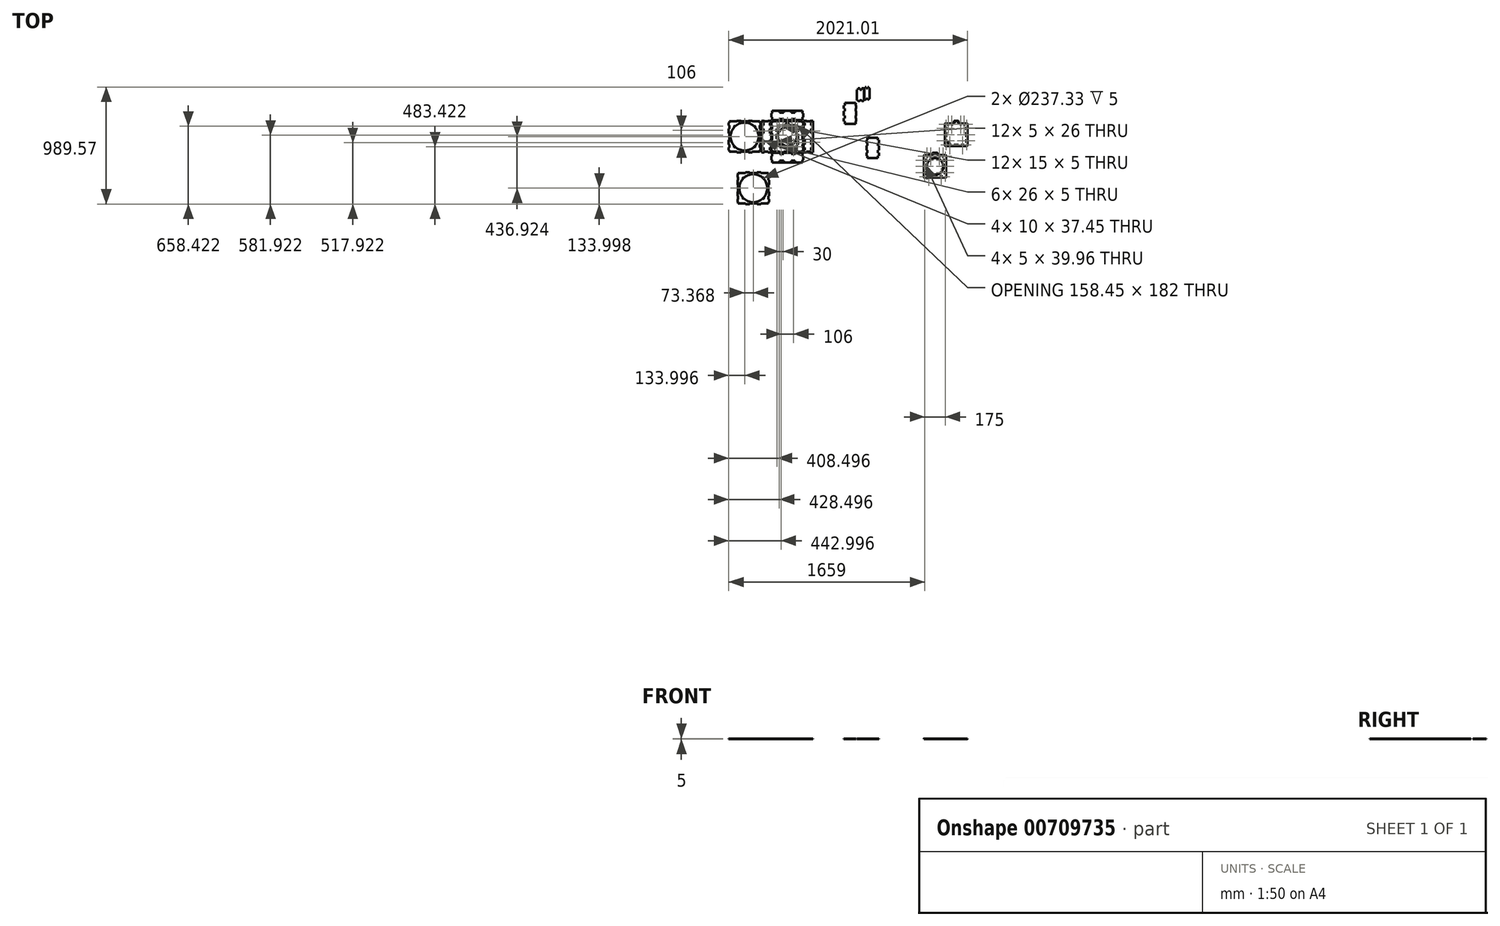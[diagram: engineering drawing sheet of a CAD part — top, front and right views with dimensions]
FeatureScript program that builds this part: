
annotation { "Feature Type Name" : "Feature", "Feature Type Description" : "" }
export const myFeature = defineFeature(function(context is Context, id is Id, definition is map)
    precondition{}
    {
        {
            var Q0;
            Q0=qCreatedBy(makeId("Top.planeOp"),FACE);
            var sketch = newSketch(context, id + "F0", { "sketchPlane" : qUnion([Q0])});
            skPoint(sketch, "E0.endSnap0", {"position": v(-875.61, -634.44) * mm});
            skArc(sketch, "E1", {"start": v(-897.61, -691.52) * mm, "mid": v(-875.61, -848.44) * mm, "end": v(-853.61, -691.52) * mm});
            skPoint(sketch, "E0.start.orphan", {"position": v(-1009.61, -768.44) * mm});
            skLineSegment(sketch, "E2", {"start": v(-875.61, -666.44) * mm, "end": v(-870.73, -666.44) * mm});
            skLineSegment(sketch, "E3", {"start": v(-875.61, -666.44) * mm, "end": v(-853.61, -666.44) * mm});
            skLineSegment(sketch, "E4", {"start": v(-853.61, -666.44) * mm, "end": v(-853.61, -691.52) * mm});
            skLineSegment(sketch, "E5", {"start": v(-897.61, -666.44) * mm, "end": v(-897.61, -691.52) * mm});
            skPoint(sketch, "E6.orphan", {"position": v(-1004.61, -634.44) * mm});
            skLineSegment(sketch, "E7", {"start": v(-1004.61, -625.24) * mm, "end": v(-1004.61, -620.24) * mm});
            skLineSegment(sketch, "E8", {"start": v(-1004.61, -565.24) * mm, "end": v(-1004.61, -555.24) * mm});
            skLineSegment(sketch, "E9", {"start": v(-746.61, -625.24) * mm, "end": v(-746.61, -604) * mm});
            skLineSegment(sketch, "E10", {"start": v(-907.86, -620.24) * mm, "end": v(-940.11, -620.24) * mm});
            skLineSegment(sketch, "E11", {"start": v(-940.11, -620.24) * mm, "end": v(-907.86, -620.24) * mm});
            skPoint(sketch, "E12.end.orphan", {"position": v(-746.61, -634.44) * mm});
            skLineSegment(sketch, "E13", {"start": v(-843.36, -620.24) * mm, "end": v(-811.11, -620.24) * mm});
            skLineSegment(sketch, "E14", {"start": v(-940.11, -620.24) * mm, "end": v(-940.11, -625.24) * mm});
            skLineSegment(sketch, "E15", {"start": v(-811.11, -620.24) * mm, "end": v(-811.11, -625.24) * mm});
            skLineSegment(sketch, "E16", {"start": v(-907.86, -620.24) * mm, "end": v(-907.86, -625.24) * mm});
            skLineSegment(sketch, "E17", {"start": v(-843.36, -620.24) * mm, "end": v(-843.36, -625.24) * mm});
            skLineSegment(sketch, "E18", {"start": v(-940.11, -634.44) * mm, "end": v(-940.11, -639.44) * mm});
            skLineSegment(sketch, "E19", {"start": v(-907.86, -634.44) * mm, "end": v(-907.86, -639.44) * mm});
            skLineSegment(sketch, "E20", {"start": v(-811.11, -634.44) * mm, "end": v(-811.11, -639.44) * mm});
            skLineSegment(sketch, "E21.trimOffspring", {"start": v(-940.11, -634.44) * mm, "end": v(-907.86, -634.44) * mm});
            skLineSegment(sketch, "E22.trimOffspring", {"start": v(-843.36, -634.44) * mm, "end": v(-811.11, -634.44) * mm});
            skPoint(sketch, "E23.orphan", {"position": v(-746.61, -620.24) * mm});
            skPoint(sketch, "E24.orphan", {"position": v(-1004.61, -620.24) * mm});
            skLineSegment(sketch, "E25.MirrorCS", {"start": v(-940.11, -916.63) * mm, "end": v(-940.11, -911.63) * mm});
            skLineSegment(sketch, "E26.MirrorCS", {"start": v(-907.86, -916.63) * mm, "end": v(-907.86, -911.63) * mm});
            skLineSegment(sketch, "E27.MirrorCS", {"start": v(-811.11, -916.63) * mm, "end": v(-811.11, -911.63) * mm});
            skLineSegment(sketch, "E28.MirrorCS", {"start": v(-843.36, -916.63) * mm, "end": v(-843.36, -911.63) * mm});
            skLineSegment(sketch, "E29.MirrorCS", {"start": v(-907.86, -916.63) * mm, "end": v(-940.11, -916.63) * mm});
            skLineSegment(sketch, "E30.MirrorCS", {"start": v(-1004.61, -971.63) * mm, "end": v(-1004.61, -981.63) * mm});
            skPoint(sketch, "E31.MirrorP", {"position": v(-1004.61, -902.44) * mm});
            skPoint(sketch, "E32.MirrorP", {"position": v(-746.61, -902.44) * mm});
            skPoint(sketch, "E33.MirrorP", {"position": v(-875.61, -911.63) * mm});
            skLineSegment(sketch, "E34.MirrorCS", {"start": v(-940.11, -916.63) * mm, "end": v(-907.86, -916.63) * mm});
            skPoint(sketch, "E35.MirrorP", {"position": v(-875.61, -902.44) * mm});
            skPoint(sketch, "E36.MirrorP", {"position": v(-746.61, -916.63) * mm});
            skPoint(sketch, "E37.MirrorP", {"position": v(-875.61, -916.63) * mm});
            skLineSegment(sketch, "E38.MirrorCS", {"start": v(-1004.61, -911.63) * mm, "end": v(-1004.61, -932.88) * mm});
            skPoint(sketch, "E39.MirrorP", {"position": v(-1004.61, -916.63) * mm});
            skLineSegment(sketch, "E40", {"start": v(-940.11, -902.44) * mm, "end": v(-940.11, -897.44) * mm});
            skLineSegment(sketch, "E41", {"start": v(-907.86, -902.44) * mm, "end": v(-907.86, -897.44) * mm});
            skLineSegment(sketch, "E42.trimOffspring", {"start": v(-843.36, -902.44) * mm, "end": v(-811.11, -902.44) * mm});
            skLineSegment(sketch, "E43.trimOffspring", {"start": v(-940.11, -897.44) * mm, "end": v(-1004.61, -897.44) * mm});
            skLineSegment(sketch, "E44", {"start": v(-907.86, -897.44) * mm, "end": v(-843.36, -897.44) * mm});
            skLineSegment(sketch, "E45", {"start": v(-843.36, -897.44) * mm, "end": v(-843.36, -902.44) * mm});
            skLineSegment(sketch, "E46", {"start": v(-811.11, -902.44) * mm, "end": v(-811.11, -897.44) * mm});
            skLineSegment(sketch, "E47", {"start": v(-811.11, -897.44) * mm, "end": v(-746.61, -897.44) * mm});
            skLineSegment(sketch, "E48.trimOffspring", {"start": v(-940.11, -902.44) * mm, "end": v(-907.86, -902.44) * mm});
            skLineSegment(sketch, "E49", {"start": v(-1022.61, -634.44) * mm, "end": v(-1038.86, -634.44) * mm});
            skLineSegment(sketch, "E50", {"start": v(-1022.61, -902.44) * mm, "end": v(-1038.86, -902.44) * mm});
            skPoint(sketch, "E51.start.orphan", {"position": v(-1017.61, -634.44) * mm});
            skPoint(sketch, "E52.end.orphan", {"position": v(-1004.61, -768.49) * mm});
            skLineSegment(sketch, "E53", {"start": v(-1004.61, -788.44) * mm, "end": v(-1004.61, -748.44) * mm});
            skLineSegment(sketch, "E54.trimOffspring", {"start": v(-1009.61, -797.41) * mm, "end": v(-1009.61, -818.44) * mm});
            skPoint(sketch, "E55.start.orphan", {"position": v(-1007.11, -788.44) * mm});
            skLineSegment(sketch, "E56", {"start": v(-1055.11, -639.54) * mm, "end": v(-1071.36, -639.54) * mm});
            skLineSegment(sketch, "E57", {"start": v(-1071.36, -639.54) * mm, "end": v(-1038.86, -639.54) * mm});
            skLineSegment(sketch, "E58", {"start": v(-1038.86, -639.54) * mm, "end": v(-1055.11, -639.54) * mm});
            skLineSegment(sketch, "E59", {"start": v(-1038.86, -639.54) * mm, "end": v(-1038.86, -634.44) * mm});
            skLineSegment(sketch, "E60", {"start": v(-1071.36, -639.54) * mm, "end": v(-1055.11, -639.54) * mm});
            skLineSegment(sketch, "E61", {"start": v(-1071.36, -639.54) * mm, "end": v(-1071.36, -634.44) * mm});
            skLineSegment(sketch, "E62.trimOffspring", {"start": v(-1071.36, -634.44) * mm, "end": v(-1087.61, -634.44) * mm});
            skPoint(sketch, "E63.orphan", {"position": v(-1087.61, -639.54) * mm});
            skPoint(sketch, "E64.orphan", {"position": v(-1022.61, -639.54) * mm});
            skLineSegment(sketch, "E65", {"start": v(-1004.61, -620.24) * mm, "end": v(-1004.61, -604) * mm});
            skLineSegment(sketch, "E66", {"start": v(-1004.61, -604) * mm, "end": v(-1009.61, -604) * mm});
            skLineSegment(sketch, "E67", {"start": v(-1009.61, -604) * mm, "end": v(-1009.61, -571.5) * mm});
            skLineSegment(sketch, "E68", {"start": v(-1009.61, -571.5) * mm, "end": v(-1004.61, -571.5) * mm});
            skLineSegment(sketch, "E69.trimOffspring", {"start": v(-1004.61, -571.5) * mm, "end": v(-1004.61, -565.24) * mm});
            skLineSegment(sketch, "E70.MirrorCS", {"start": v(-1004.61, -932.88) * mm, "end": v(-1009.61, -932.88) * mm});
            skLineSegment(sketch, "E71.MirrorCS", {"start": v(-1009.61, -932.88) * mm, "end": v(-1009.61, -965.38) * mm});
            skLineSegment(sketch, "E72.MirrorCS", {"start": v(-1009.61, -965.38) * mm, "end": v(-1004.61, -965.38) * mm});
            skLineSegment(sketch, "E73.MirrorCS", {"start": v(-1071.36, -897.44) * mm, "end": v(-1038.86, -897.44) * mm});
            skLineSegment(sketch, "E74.MirrorCS", {"start": v(-1071.36, -897.44) * mm, "end": v(-1071.36, -902.44) * mm});
            skLineSegment(sketch, "E75.MirrorCS", {"start": v(-1038.86, -897.44) * mm, "end": v(-1038.86, -902.44) * mm});
            skLineSegment(sketch, "E76.trimOffspring", {"start": v(-1071.36, -902.44) * mm, "end": v(-1087.61, -902.44) * mm});
            skLineSegment(sketch, "E77", {"start": v(-1237.61, -646.69) * mm, "end": v(-1237.61, -644.69) * mm});
            skCircle(sketch, "E78", {"center": v(-1237.61, -644.69) * mm, "radius": 2 * mm});
            skCircle(sketch, "E79", {"center": v(-1237.61, -892.19) * mm, "radius": 2 * mm});
            skCircle(sketch, "E80", {"center": v(-1325.12, -680.93) * mm, "radius": 2 * mm});
            skCircle(sketch, "E81.MirrorC", {"center": v(-1325.12, -855.94) * mm, "radius": 2 * mm});
            skPoint(sketch, "E82.orphan", {"position": v(-1237.61, -768.44) * mm});
            skLineSegment(sketch, "E83.trimOffspring", {"start": v(-1004.61, -965.38) * mm, "end": v(-1004.61, -971.63) * mm});
            skLineSegment(sketch, "E84", {"start": v(-1087.61, -702.02) * mm, "end": v(-1082.61, -702.02) * mm});
            skLineSegment(sketch, "E85", {"start": v(-1087.61, -739.46) * mm, "end": v(-1082.61, -739.46) * mm});
            skLineSegment(sketch, "E86", {"start": v(-1087.61, -884.78) * mm, "end": v(-1082.61, -884.78) * mm});
            skLineSegment(sketch, "E87", {"start": v(-1087.61, -834.86) * mm, "end": v(-1082.61, -834.86) * mm});
            skLineSegment(sketch, "E88", {"start": v(-1087.61, -797.41) * mm, "end": v(-1082.61, -797.41) * mm});
            skLineSegment(sketch, "E89", {"start": v(-1087.61, -862.25) * mm, "end": v(-1082.61, -862.25) * mm});
            skPoint(sketch, "E90.orphan", {"position": v(-1082.61, -902.44) * mm});
            skLineSegment(sketch, "E91.MirrorCS", {"start": v(-741.61, -604) * mm, "end": v(-741.61, -571.5) * mm});
            skLineSegment(sketch, "E92.MirrorCS", {"start": v(-746.61, -604) * mm, "end": v(-741.61, -604) * mm});
            skLineSegment(sketch, "E93.MirrorCS", {"start": v(-741.61, -571.5) * mm, "end": v(-746.61, -571.5) * mm});
            skLineSegment(sketch, "E94.trimOffspring", {"start": v(-746.61, -571.5) * mm, "end": v(-746.61, -555.24) * mm});
            skLineSegment(sketch, "E95.MirrorCS", {"start": v(-1366.61, -897.44) * mm, "end": v(-1302.11, -897.44) * mm});
            skLineSegment(sketch, "E96.MirrorCS", {"start": v(-1302.11, -902.44) * mm, "end": v(-1302.11, -897.44) * mm});
            skLineSegment(sketch, "E97.MirrorCS", {"start": v(-1302.11, -902.44) * mm, "end": v(-1269.86, -902.44) * mm});
            skLineSegment(sketch, "E98.MirrorCS", {"start": v(-1269.86, -902.44) * mm, "end": v(-1269.86, -897.44) * mm});
            skPoint(sketch, "E99.orphan", {"position": v(-1237.61, -736.59) * mm});
            skLineSegment(sketch, "E100", {"start": v(-940.11, -560.24) * mm, "end": v(-940.11, -555.24) * mm});
            skLineSegment(sketch, "E101", {"start": v(-907.86, -560.24) * mm, "end": v(-907.86, -555.24) * mm});
            skLineSegment(sketch, "E102", {"start": v(-811.11, -560.24) * mm, "end": v(-811.11, -555.24) * mm});
            skLineSegment(sketch, "E103", {"start": v(-843.36, -560.24) * mm, "end": v(-843.36, -555.24) * mm});
            skPoint(sketch, "E104.orphan", {"position": v(-747.11, -560.24) * mm});
            skPoint(sketch, "E105.MirrorP", {"position": v(-746.61, -768.44) * mm});
            skLineSegment(sketch, "E106.MirrorCS", {"start": v(-746.61, -911.63) * mm, "end": v(-746.61, -932.88) * mm});
            skLineSegment(sketch, "E107.MirrorCS", {"start": v(-746.61, -965.38) * mm, "end": v(-746.61, -981.63) * mm});
            skLineSegment(sketch, "E108.MirrorCS", {"start": v(-811.11, -976.63) * mm, "end": v(-811.11, -981.63) * mm});
            skLineSegment(sketch, "E109.MirrorCS", {"start": v(-907.86, -976.63) * mm, "end": v(-907.86, -981.63) * mm});
            skLineSegment(sketch, "E110.MirrorCS", {"start": v(-843.36, -976.63) * mm, "end": v(-843.36, -981.63) * mm});
            skLineSegment(sketch, "E111.MirrorCS", {"start": v(-940.11, -976.63) * mm, "end": v(-940.11, -981.63) * mm});
            skPoint(sketch, "E112.MirrorP", {"position": v(-1017.61, -902.44) * mm});
            skPoint(sketch, "E113.MirrorP", {"position": v(-747.11, -916.63) * mm});
            skPoint(sketch, "E114.MirrorP", {"position": v(-1087.61, -897.44) * mm});
            skLineSegment(sketch, "E115.MirrorCS", {"start": v(-741.61, -932.88) * mm, "end": v(-741.61, -965.38) * mm});
            skPoint(sketch, "E116.MirrorP", {"position": v(-1022.61, -897.44) * mm});
            skPoint(sketch, "E117.MirrorP", {"position": v(-1055.11, -902.44) * mm});
            skPoint(sketch, "E118.MirrorP", {"position": v(-746.61, -976.63) * mm});
            skLineSegment(sketch, "E119.MirrorCS", {"start": v(-747.11, -911.63) * mm, "end": v(-746.61, -911.63) * mm});
            skLineSegment(sketch, "E120.trimOffspring", {"start": v(-741.61, -718.44) * mm, "end": v(-741.61, -739.46) * mm});
            skLineSegment(sketch, "E121.trimOffspring", {"start": v(-746.61, -788.34) * mm, "end": v(-746.61, -748.44) * mm});
            skPoint(sketch, "E122.end.orphan", {"position": v(-875.61, -736.59) * mm});
            skPoint(sketch, "E123.end.orphan", {"position": v(-911.85, -768.44) * mm});
            skLineSegment(sketch, "E124.trimOffspring", {"start": v(-1004.61, -571.5) * mm, "end": v(-1004.61, -555.24) * mm});
            skPoint(sketch, "E125.trimOffspring.end.orphan", {"position": v(-1017.61, -678.44) * mm});
            skPoint(sketch, "E126.start.orphan", {"position": v(-1056.61, -736.59) * mm});
            skPoint(sketch, "E127.end.orphan", {"position": v(-1022.61, -818.44) * mm});
            skPoint(sketch, "E128.start.orphan", {"position": v(-1009.61, -718.44) * mm});
            skPoint(sketch, "E129.end.orphan", {"position": v(-1022.61, -718.44) * mm});
            skLineSegment(sketch, "E130", {"start": v(-875.61, -768.44) * mm, "end": v(-875.61, -736.59) * mm});
            skLineSegment(sketch, "E131.MirrorCS", {"start": v(-1009.61, -788.34) * mm, "end": v(-1009.61, -788.44) * mm});
            skLineSegment(sketch, "E132.MirrorCS", {"start": v(-1004.61, -788.34) * mm, "end": v(-1004.61, -748.44) * mm});
            skLineSegment(sketch, "E133.MirrorCS", {"start": v(-1087.61, -652.1) * mm, "end": v(-1082.61, -652.1) * mm});
            skLineSegment(sketch, "E134.MirrorCS", {"start": v(-1087.61, -674.63) * mm, "end": v(-1082.61, -674.63) * mm});
            skLineSegment(sketch, "E135", {"start": v(-1366.61, -674.63) * mm, "end": v(-1366.61, -702.02) * mm});
            skLineSegment(sketch, "E136", {"start": v(-1366.61, -702.02) * mm, "end": v(-1371.61, -702.02) * mm});
            skLineSegment(sketch, "E137", {"start": v(-1371.61, -702.02) * mm, "end": v(-1371.61, -739.46) * mm});
            skLineSegment(sketch, "E138", {"start": v(-1371.61, -739.46) * mm, "end": v(-1366.61, -739.46) * mm});
            skLineSegment(sketch, "E139", {"start": v(-1366.61, -739.46) * mm, "end": v(-1366.61, -797.41) * mm});
            skLineSegment(sketch, "E140", {"start": v(-1366.61, -797.41) * mm, "end": v(-1371.61, -797.41) * mm});
            skLineSegment(sketch, "E141", {"start": v(-1371.61, -797.41) * mm, "end": v(-1371.61, -834.86) * mm});
            skLineSegment(sketch, "E142", {"start": v(-1371.61, -834.86) * mm, "end": v(-1366.61, -834.86) * mm});
            skLineSegment(sketch, "E143", {"start": v(-1366.61, -834.86) * mm, "end": v(-1366.61, -862.25) * mm});
            skLineSegment(sketch, "E144", {"start": v(-1366.61, -862.25) * mm, "end": v(-1371.61, -862.25) * mm});
            skLineSegment(sketch, "E145", {"start": v(-1371.61, -862.25) * mm, "end": v(-1371.61, -884.78) * mm});
            skLineSegment(sketch, "E146", {"start": v(-1371.61, -884.78) * mm, "end": v(-1366.61, -884.78) * mm});
            skLineSegment(sketch, "E147", {"start": v(-1366.61, -884.78) * mm, "end": v(-1366.61, -897.44) * mm});
            skLineSegment(sketch, "E148", {"start": v(-1237.61, -768.44) * mm, "end": v(-1237.61, -748.8) * mm});
            skLineSegment(sketch, "E149.MirrorCS", {"start": v(-1108.61, -674.63) * mm, "end": v(-1108.61, -702.02) * mm});
            skLineSegment(sketch, "E150.MirrorCS", {"start": v(-1108.61, -702.02) * mm, "end": v(-1103.61, -702.02) * mm});
            skLineSegment(sketch, "E151.MirrorCS", {"start": v(-1103.61, -702.02) * mm, "end": v(-1103.61, -739.46) * mm});
            skLineSegment(sketch, "E152.MirrorCS", {"start": v(-1103.61, -739.46) * mm, "end": v(-1108.61, -739.46) * mm});
            skLineSegment(sketch, "E153.MirrorCS", {"start": v(-1108.61, -739.46) * mm, "end": v(-1108.61, -797.41) * mm});
            skLineSegment(sketch, "E154.MirrorCS", {"start": v(-1108.61, -797.41) * mm, "end": v(-1103.61, -797.41) * mm});
            skLineSegment(sketch, "E155.MirrorCS", {"start": v(-1103.61, -797.41) * mm, "end": v(-1103.61, -834.86) * mm});
            skLineSegment(sketch, "E156.MirrorCS", {"start": v(-1103.61, -834.86) * mm, "end": v(-1108.61, -834.86) * mm});
            skLineSegment(sketch, "E157.MirrorCS", {"start": v(-1108.61, -834.86) * mm, "end": v(-1108.61, -862.25) * mm});
            skLineSegment(sketch, "E158.MirrorCS", {"start": v(-1108.61, -862.25) * mm, "end": v(-1103.61, -862.25) * mm});
            skLineSegment(sketch, "E159.MirrorCS", {"start": v(-1103.61, -862.25) * mm, "end": v(-1103.61, -884.78) * mm});
            skLineSegment(sketch, "E160.MirrorCS", {"start": v(-1103.61, -884.78) * mm, "end": v(-1108.61, -884.78) * mm});
            skLineSegment(sketch, "E161.MirrorCS", {"start": v(-1108.61, -897.44) * mm, "end": v(-1173.11, -897.44) * mm});
            skLineSegment(sketch, "E162.MirrorCS", {"start": v(-1173.11, -902.44) * mm, "end": v(-1173.11, -897.44) * mm});
            skLineSegment(sketch, "E163.MirrorCS", {"start": v(-1173.11, -902.44) * mm, "end": v(-1205.36, -902.44) * mm});
            skLineSegment(sketch, "E164.MirrorCS", {"start": v(-1205.36, -902.44) * mm, "end": v(-1205.36, -897.44) * mm});
            skLineSegment(sketch, "E165", {"start": v(-1269.86, -897.44) * mm, "end": v(-1205.36, -897.44) * mm});
            skLineSegment(sketch, "E166", {"start": v(-1108.61, -884.78) * mm, "end": v(-1108.61, -897.44) * mm});
            skCircle(sketch, "E167", {"center": v(-940.63, -837.56) * mm, "radius": 7.1 * mm});
            skLineSegment(sketch, "E168", {"start": v(-1237.61, -768.44) * mm, "end": v(-1301.14, -768.44) * mm});
            skLineSegment(sketch, "E169.MirrorCS", {"start": v(-1371.61, -652.1) * mm, "end": v(-1366.61, -652.1) * mm});
            skLineSegment(sketch, "E170.MirrorCS", {"start": v(-1366.61, -674.63) * mm, "end": v(-1371.61, -674.63) * mm});
            skLineSegment(sketch, "E171.MirrorCS", {"start": v(-1366.61, -702.02) * mm, "end": v(-1366.61, -674.63) * mm});
            skLineSegment(sketch, "E172.MirrorCS", {"start": v(-1366.61, -652.1) * mm, "end": v(-1366.61, -639.44) * mm});
            skLineSegment(sketch, "E173.MirrorCS", {"start": v(-1366.61, -639.44) * mm, "end": v(-1302.11, -639.44) * mm});
            skLineSegment(sketch, "E174.MirrorCS", {"start": v(-1302.11, -634.44) * mm, "end": v(-1302.11, -639.44) * mm});
            skLineSegment(sketch, "E175.MirrorCS", {"start": v(-1302.11, -634.44) * mm, "end": v(-1269.86, -634.44) * mm});
            skLineSegment(sketch, "E176.MirrorCS", {"start": v(-1173.11, -634.44) * mm, "end": v(-1205.36, -634.44) * mm});
            skLineSegment(sketch, "E177.MirrorCS", {"start": v(-1173.11, -634.44) * mm, "end": v(-1173.11, -639.44) * mm});
            skLineSegment(sketch, "E178.MirrorCS", {"start": v(-1108.61, -639.44) * mm, "end": v(-1173.11, -639.44) * mm});
            skLineSegment(sketch, "E179.MirrorCS", {"start": v(-1108.61, -652.1) * mm, "end": v(-1108.61, -639.44) * mm});
            skLineSegment(sketch, "E180.MirrorCS", {"start": v(-1103.61, -652.1) * mm, "end": v(-1108.61, -652.1) * mm});
            skLineSegment(sketch, "E181.MirrorCS", {"start": v(-1103.61, -674.63) * mm, "end": v(-1103.61, -652.1) * mm});
            skLineSegment(sketch, "E182.MirrorCS", {"start": v(-1108.61, -674.63) * mm, "end": v(-1103.61, -674.63) * mm});
            skLineSegment(sketch, "E183.MirrorCS", {"start": v(-1108.61, -702.02) * mm, "end": v(-1108.61, -674.63) * mm});
            skLineSegment(sketch, "E184.MirrorCS", {"start": v(-1103.61, -702.02) * mm, "end": v(-1108.61, -702.02) * mm});
            skLineSegment(sketch, "E185.MirrorCS", {"start": v(-1103.61, -739.46) * mm, "end": v(-1103.61, -702.02) * mm});
            skLineSegment(sketch, "E186.MirrorCS", {"start": v(-1269.86, -639.44) * mm, "end": v(-1205.36, -639.44) * mm});
            skLineSegment(sketch, "E187.MirrorCS", {"start": v(-1269.86, -634.44) * mm, "end": v(-1269.86, -639.44) * mm});
            skLineSegment(sketch, "E188.MirrorCS", {"start": v(-1205.36, -634.44) * mm, "end": v(-1205.36, -639.44) * mm});
            skLineSegment(sketch, "E189.MirrorCS", {"start": v(-1371.61, -674.63) * mm, "end": v(-1371.61, -652.1) * mm});
            skCircle(sketch, "E190.MirrorC", {"center": v(-1150.1, -680.93) * mm, "radius": 2 * mm});
            skCircle(sketch, "E191.MirrorC", {"center": v(-1150.1, -855.94) * mm, "radius": 2 * mm});
            skLineSegment(sketch, "E192", {"start": v(-1237.61, -768.44) * mm, "end": v(-1333.51, -768.44) * mm});
            skCircle(sketch, "E193", {"center": v(-1361.36, -768.44) * mm, "radius": 2 * mm});
            skCircle(sketch, "E194", {"center": v(-1237.61, -768.44) * mm, "radius": 118.66 * mm});
            skPoint(sketch, "E195.trimOffspring.end.orphan", {"position": v(-1366.61, -768.44) * mm});
            skCircle(sketch, "E196.MirrorC", {"center": v(-1113.86, -768.44) * mm, "radius": 2 * mm});
            skLineSegment(sketch, "E197", {"start": v(-843.36, -916.63) * mm, "end": v(-811.11, -916.63) * mm});
            skLineSegment(sketch, "E198", {"start": v(-746.61, -965.38) * mm, "end": v(-741.61, -965.38) * mm});
            skLineSegment(sketch, "E199", {"start": v(-746.61, -932.88) * mm, "end": v(-741.61, -932.88) * mm});
            skLineSegment(sketch, "E200", {"start": v(-875.61, -768.44) * mm, "end": v(-844.99, -768.44) * mm});
            skPoint(sketch, "E201.MirrorCS.end.orphan", {"position": v(-747.11, -565.24) * mm});
            skLineSegment(sketch, "E202", {"start": v(-907.86, -639.44) * mm, "end": v(-843.36, -639.44) * mm});
            skPoint(sketch, "E203.orphan", {"position": v(-746.61, -639.54) * mm});
            skLineSegment(sketch, "E204.trimOffspring", {"start": v(-811.11, -639.44) * mm, "end": v(-746.61, -639.44) * mm});
            skLineSegment(sketch, "E205", {"start": v(-843.36, -639.44) * mm, "end": v(-843.36, -634.44) * mm});
            skLineSegment(sketch, "E206", {"start": v(-940.11, -639.44) * mm, "end": v(-1004.61, -639.44) * mm});
            skPoint(sketch, "E207.orphan", {"position": v(-1004.61, -639.54) * mm});
            skLineSegment(sketch, "E208", {"start": v(-940.11, -630.24) * mm, "end": v(-746.61, -630.24) * mm});
            skLineSegment(sketch, "E209.bottom", {"start": v(-746.61, -630.24) * mm, "end": v(-1004.61, -630.24) * mm});
            skLineSegment(sketch, "E209.top", {"start": v(-811.11, -625.24) * mm, "end": v(-843.36, -625.24) * mm});
            skLineSegment(sketch, "E209.left", {"start": v(-746.61, -630.24) * mm, "end": v(-746.61, -625.24) * mm});
            skLineSegment(sketch, "E209.right", {"start": v(-1004.61, -630.24) * mm, "end": v(-1004.61, -625.24) * mm});
            skLineSegment(sketch, "E210.trimOffspring", {"start": v(-907.86, -625.24) * mm, "end": v(-940.11, -625.24) * mm});
            skPoint(sketch, "E211.orphan", {"position": v(-875.61, -625.24) * mm});
            skLineSegment(sketch, "E212.MirrorCS", {"start": v(-907.86, -555.24) * mm, "end": v(-940.11, -555.24) * mm});
            skLineSegment(sketch, "E213.MirrorCS", {"start": v(-746.61, -550.24) * mm, "end": v(-1004.61, -550.24) * mm});
            skLineSegment(sketch, "E214.MirrorCS", {"start": v(-1004.61, -550.24) * mm, "end": v(-1004.61, -555.24) * mm});
            skLineSegment(sketch, "E215.MirrorCS", {"start": v(-746.61, -550.24) * mm, "end": v(-746.61, -555.24) * mm});
            skLineSegment(sketch, "E216.MirrorCS", {"start": v(-811.11, -555.24) * mm, "end": v(-843.36, -555.24) * mm});
            skPoint(sketch, "E217.start.orphan", {"position": v(-940.11, -590.24) * mm});
            skLineSegment(sketch, "E218.MirrorCS", {"start": v(-746.61, -906.63) * mm, "end": v(-1004.61, -906.63) * mm});
            skLineSegment(sketch, "E219.MirrorCS", {"start": v(-907.86, -911.63) * mm, "end": v(-940.11, -911.63) * mm});
            skLineSegment(sketch, "E220.MirrorCS", {"start": v(-1004.61, -906.63) * mm, "end": v(-1004.61, -911.63) * mm});
            skLineSegment(sketch, "E221.MirrorCS", {"start": v(-811.11, -911.63) * mm, "end": v(-843.36, -911.63) * mm});
            skLineSegment(sketch, "E222.MirrorCS", {"start": v(-746.61, -906.63) * mm, "end": v(-746.61, -911.63) * mm});
            skLineSegment(sketch, "E223.MirrorCS", {"start": v(-746.61, -986.63) * mm, "end": v(-746.61, -981.63) * mm});
            skLineSegment(sketch, "E224.MirrorCS", {"start": v(-746.61, -986.63) * mm, "end": v(-1004.61, -986.63) * mm});
            skLineSegment(sketch, "E225.MirrorCS", {"start": v(-811.11, -981.63) * mm, "end": v(-843.36, -981.63) * mm});
            skLineSegment(sketch, "E226.MirrorCS", {"start": v(-907.86, -981.63) * mm, "end": v(-940.11, -981.63) * mm});
            skLineSegment(sketch, "E227.MirrorCS", {"start": v(-1004.61, -986.63) * mm, "end": v(-1004.61, -981.63) * mm});
            skPoint(sketch, "E228.end.orphan", {"position": v(-738.61, -902.44) * mm});
            skLineSegment(sketch, "E229.MirrorCS", {"start": v(-1092.61, -634.44) * mm, "end": v(-1092.61, -902.44) * mm});
            skLineSegment(sketch, "E230.MirrorCS", {"start": v(-1087.61, -634.44) * mm, "end": v(-1092.61, -634.44) * mm});
            skLineSegment(sketch, "E231.MirrorCS", {"start": v(-1087.61, -674.63) * mm, "end": v(-1087.61, -652.1) * mm});
            skLineSegment(sketch, "E232.MirrorCS", {"start": v(-1087.61, -739.46) * mm, "end": v(-1087.61, -702.02) * mm});
            skLineSegment(sketch, "E233.MirrorCS", {"start": v(-1012.61, -858.44) * mm, "end": v(-1012.61, -678.44) * mm});
            skLineSegment(sketch, "E234.MirrorCS", {"start": v(-1087.61, -834.86) * mm, "end": v(-1087.61, -797.41) * mm});
            skLineSegment(sketch, "E235.MirrorCS", {"start": v(-1087.61, -862.25) * mm, "end": v(-1087.61, -884.78) * mm});
            skLineSegment(sketch, "E236.MirrorCS", {"start": v(-1092.61, -902.44) * mm, "end": v(-1087.61, -902.44) * mm});
            skPoint(sketch, "E237.MirrorCS.start.orphan", {"position": v(-1017.61, -748.44) * mm});
            skPoint(sketch, "E238.MirrorCS.start.orphan", {"position": v(-1017.61, -718.44) * mm});
            skLineSegment(sketch, "E239.MirrorCS", {"start": v(-1017.61, -902.44) * mm, "end": v(-1022.61, -902.44) * mm});
            skPoint(sketch, "E240.MirrorCS.end.orphan", {"position": v(-1022.61, -748.44) * mm});
            skLineSegment(sketch, "E241", {"start": v(-1022.61, -652.1) * mm, "end": v(-1017.61, -652.1) * mm});
            skLineSegment(sketch, "E242", {"start": v(-1022.61, -634.44) * mm, "end": v(-1017.61, -634.44) * mm});
            skLineSegment(sketch, "E243", {"start": v(-1012.61, -858.44) * mm, "end": v(-1012.61, -902.44) * mm});
            skPoint(sketch, "E243.endSnap0", {"position": v(-1020.11, -902.44) * mm});
            skLineSegment(sketch, "E244", {"start": v(-1012.61, -902.44) * mm, "end": v(-1022.61, -902.44) * mm});
            skLineSegment(sketch, "E245", {"start": v(-1012.61, -678.44) * mm, "end": v(-1012.61, -634.44) * mm});
            skLineSegment(sketch, "E246", {"start": v(-1012.61, -634.44) * mm, "end": v(-1017.61, -634.44) * mm});
            skLineSegment(sketch, "E247", {"start": v(-1017.61, -652.1) * mm, "end": v(-1017.61, -674.63) * mm});
            skPoint(sketch, "E248.MirrorCS.start.orphan", {"position": v(-1012.61, -858.44) * mm});
            skLineSegment(sketch, "E249", {"start": v(-1022.61, -884.78) * mm, "end": v(-1017.61, -884.78) * mm});
            skLineSegment(sketch, "E250", {"start": v(-1022.61, -862.25) * mm, "end": v(-1017.61, -862.25) * mm});
            skLineSegment(sketch, "E251", {"start": v(-1022.61, -834.86) * mm, "end": v(-1017.61, -834.86) * mm});
            skLineSegment(sketch, "E252", {"start": v(-1022.61, -797.41) * mm, "end": v(-1017.61, -797.41) * mm});
            skLineSegment(sketch, "E253", {"start": v(-1022.61, -739.46) * mm, "end": v(-1017.61, -739.46) * mm});
            skLineSegment(sketch, "E254", {"start": v(-1022.61, -702.02) * mm, "end": v(-1017.61, -702.02) * mm});
            skLineSegment(sketch, "E255", {"start": v(-1022.61, -674.63) * mm, "end": v(-1017.61, -674.63) * mm});
            skPoint(sketch, "E256.orphan", {"position": v(-1022.61, -678.44) * mm});
            skPoint(sketch, "E257.MirrorCS.end.orphan", {"position": v(-1012.61, -678.44) * mm});
            skPoint(sketch, "E258.MirrorCS.start.orphan", {"position": v(-1022.61, -634.44) * mm});
            skPoint(sketch, "E259.MirrorCS.end.orphan", {"position": v(-1022.61, -652.1) * mm});
            skPoint(sketch, "E260.MirrorCS.start.orphan", {"position": v(-1022.61, -674.63) * mm});
            skPoint(sketch, "E261.orphan", {"position": v(-1022.61, -739.46) * mm});
            skPoint(sketch, "E262.MirrorCS.end.orphan", {"position": v(-1022.61, -702.02) * mm});
            skPoint(sketch, "E263.MirrorCS.end.orphan", {"position": v(-1022.61, -797.41) * mm});
            skPoint(sketch, "E264.MirrorCS.end.orphan", {"position": v(-1022.61, -902.44) * mm});
            skLineSegment(sketch, "E265", {"start": v(-1017.61, -862.25) * mm, "end": v(-1017.61, -884.78) * mm});
            skLineSegment(sketch, "E266", {"start": v(-1017.61, -702.02) * mm, "end": v(-1017.61, -718.44) * mm});
            skLineSegment(sketch, "E267", {"start": v(-1082.61, -652.1) * mm, "end": v(-1077.61, -652.1) * mm});
            skLineSegment(sketch, "E268", {"start": v(-1077.61, -652.1) * mm, "end": v(-1077.61, -674.63) * mm});
            skLineSegment(sketch, "E269", {"start": v(-1077.61, -674.63) * mm, "end": v(-1082.61, -674.63) * mm});
            skLineSegment(sketch, "E270", {"start": v(-1082.61, -702.02) * mm, "end": v(-1077.61, -702.02) * mm});
            skLineSegment(sketch, "E271", {"start": v(-1077.61, -702.02) * mm, "end": v(-1077.61, -739.46) * mm});
            skLineSegment(sketch, "E272", {"start": v(-1077.61, -739.46) * mm, "end": v(-1082.61, -739.46) * mm});
            skLineSegment(sketch, "E273", {"start": v(-1082.61, -797.41) * mm, "end": v(-1077.61, -797.41) * mm});
            skLineSegment(sketch, "E274", {"start": v(-1077.61, -797.41) * mm, "end": v(-1077.61, -834.86) * mm});
            skLineSegment(sketch, "E275", {"start": v(-1077.61, -834.86) * mm, "end": v(-1082.61, -834.86) * mm});
            skLineSegment(sketch, "E276", {"start": v(-1082.61, -862.25) * mm, "end": v(-1077.61, -862.25) * mm});
            skLineSegment(sketch, "E277", {"start": v(-1077.61, -862.25) * mm, "end": v(-1077.61, -884.78) * mm});
            skLineSegment(sketch, "E278", {"start": v(-1077.61, -884.78) * mm, "end": v(-1082.61, -884.78) * mm});
            skPoint(sketch, "E279.MirrorCS.end.orphan", {"position": v(-1082.61, -674.63) * mm});
            skLineSegment(sketch, "E280", {"start": v(-1022.61, -674.63) * mm, "end": v(-1022.61, -652.1) * mm});
            skLineSegment(sketch, "E281", {"start": v(-1022.61, -702.02) * mm, "end": v(-1022.61, -739.46) * mm});
            skLineSegment(sketch, "E282", {"start": v(-1022.61, -797.41) * mm, "end": v(-1022.61, -834.86) * mm});
            skLineSegment(sketch, "E283", {"start": v(-1022.61, -862.25) * mm, "end": v(-1022.61, -884.78) * mm});
            skPoint(sketch, "E284.MirrorCS.end.orphan", {"position": v(-1027.61, -884.78) * mm});
            skPoint(sketch, "E285.MirrorCS.start.orphan", {"position": v(-1027.61, -862.25) * mm});
            skPoint(sketch, "E286.MirrorCS.end.orphan", {"position": v(-1027.61, -834.86) * mm});
            skPoint(sketch, "E287.MirrorCS.start.orphan", {"position": v(-1027.61, -797.41) * mm});
            skPoint(sketch, "E288.MirrorCS.end.orphan", {"position": v(-1027.61, -652.1) * mm});
            skPoint(sketch, "E289.MirrorCS.end.orphan", {"position": v(-1027.61, -674.63) * mm});
            skPoint(sketch, "E290.MirrorCS.end.orphan", {"position": v(-1027.61, -702.02) * mm});
            skPoint(sketch, "E291.MirrorCS.end.orphan", {"position": v(-1027.61, -739.46) * mm});
            skLineSegment(sketch, "E292", {"start": v(-1009.61, -674.63) * mm, "end": v(-1004.61, -674.63) * mm});
            skLineSegment(sketch, "E293", {"start": v(-1004.61, -674.63) * mm, "end": v(-1004.61, -678.44) * mm});
            skLineSegment(sketch, "E294", {"start": v(-1009.61, -652.1) * mm, "end": v(-1004.61, -652.1) * mm});
            skLineSegment(sketch, "E295", {"start": v(-1004.61, -652.1) * mm, "end": v(-1004.61, -639.44) * mm});
            skPoint(sketch, "E296.orphan", {"position": v(-1009.61, -634.44) * mm});
            skLineSegment(sketch, "E297", {"start": v(-1009.61, -652.1) * mm, "end": v(-1009.61, -674.63) * mm});
            skPoint(sketch, "E298.start.orphan", {"position": v(-1009.61, -678.44) * mm});
            skLineSegment(sketch, "E299", {"start": v(-1009.61, -718.44) * mm, "end": v(-1009.61, -702.02) * mm});
            skLineSegment(sketch, "E300", {"start": v(-1009.61, -702.02) * mm, "end": v(-1004.61, -702.02) * mm});
            skLineSegment(sketch, "E301", {"start": v(-1009.61, -718.44) * mm, "end": v(-1009.61, -739.46) * mm});
            skLineSegment(sketch, "E302", {"start": v(-1009.61, -739.46) * mm, "end": v(-1004.61, -739.46) * mm});
            skLineSegment(sketch, "E303", {"start": v(-1004.61, -739.46) * mm, "end": v(-1004.61, -748.44) * mm});
            skPoint(sketch, "E304.MirrorCS.end.orphan", {"position": v(-1009.61, -748.44) * mm});
            skPoint(sketch, "E304.MirrorCS.start.orphan", {"position": v(-1004.61, -748.44) * mm});
            skPoint(sketch, "E305.orphan", {"position": v(-1004.61, -718.44) * mm});
            skLineSegment(sketch, "E306", {"start": v(-1004.61, -678.44) * mm, "end": v(-1004.61, -702.02) * mm});
            skLineSegment(sketch, "E307", {"start": v(-1009.61, -818.44) * mm, "end": v(-1009.61, -797.41) * mm});
            skLineSegment(sketch, "E308", {"start": v(-1009.61, -797.41) * mm, "end": v(-1004.61, -797.41) * mm});
            skLineSegment(sketch, "E309", {"start": v(-1004.61, -797.41) * mm, "end": v(-1004.61, -788.34) * mm});
            skPoint(sketch, "E310.orphan", {"position": v(-1009.61, -788.44) * mm});
            skPoint(sketch, "E311.MirrorCS.start.orphan", {"position": v(-1009.61, -788.34) * mm});
            skPoint(sketch, "E312.start.orphan", {"position": v(-1009.61, -834.86) * mm});
            skLineSegment(sketch, "E313", {"start": v(-1009.61, -818.44) * mm, "end": v(-1009.61, -834.86) * mm});
            skLineSegment(sketch, "E314", {"start": v(-1009.61, -834.86) * mm, "end": v(-1004.61, -834.86) * mm});
            skPoint(sketch, "E315.MirrorCS.end.orphan", {"position": v(-1004.61, -818.44) * mm});
            skPoint(sketch, "E315.MirrorCS.start.orphan", {"position": v(-1009.61, -818.44) * mm});
            skLineSegment(sketch, "E316", {"start": v(-1017.61, -797.41) * mm, "end": v(-1017.61, -834.86) * mm});
            skLineSegment(sketch, "E317", {"start": v(-1004.61, -834.86) * mm, "end": v(-1004.61, -858.44) * mm});
            skLineSegment(sketch, "E318", {"start": v(-1009.61, -862.25) * mm, "end": v(-1004.61, -862.25) * mm});
            skLineSegment(sketch, "E319", {"start": v(-1004.61, -862.25) * mm, "end": v(-1004.61, -858.44) * mm});
            skLineSegment(sketch, "E320", {"start": v(-1009.61, -862.25) * mm, "end": v(-1009.61, -884.78) * mm});
            skLineSegment(sketch, "E321", {"start": v(-1009.61, -884.78) * mm, "end": v(-1004.61, -884.78) * mm});
            skLineSegment(sketch, "E322", {"start": v(-1004.61, -884.78) * mm, "end": v(-1004.61, -897.44) * mm});
            skPoint(sketch, "E323.orphan", {"position": v(-1009.61, -902.44) * mm});
            skLineSegment(sketch, "E324", {"start": v(-1017.61, -702.02) * mm, "end": v(-1017.61, -739.46) * mm});
            skPoint(sketch, "E325.end.orphan", {"position": v(-738.61, -678.44) * mm});
            skPoint(sketch, "E325.start.orphan", {"position": v(-733.61, -678.44) * mm});
            skPoint(sketch, "E326.end.orphan", {"position": v(-733.61, -718.44) * mm});
            skPoint(sketch, "E326.start.orphan", {"position": v(-733.61, -748.44) * mm});
            skPoint(sketch, "E327.start.orphan", {"position": v(-738.61, -858.44) * mm});
            skLineSegment(sketch, "E328.MirrorCS", {"start": v(-679.86, -639.54) * mm, "end": v(-679.86, -634.44) * mm});
            skLineSegment(sketch, "E329.MirrorCS", {"start": v(-679.86, -897.44) * mm, "end": v(-679.86, -902.44) * mm});
            skLineSegment(sketch, "E330.MirrorCS", {"start": v(-712.36, -639.54) * mm, "end": v(-712.36, -634.44) * mm});
            skLineSegment(sketch, "E331.MirrorCS", {"start": v(-712.36, -897.44) * mm, "end": v(-712.36, -902.44) * mm});
            skPoint(sketch, "E332.MirrorP", {"position": v(-723.61, -884.78) * mm});
            skLineSegment(sketch, "E333.MirrorCS", {"start": v(-668.61, -652.1) * mm, "end": v(-673.61, -652.1) * mm});
            skLineSegment(sketch, "E334.MirrorCS", {"start": v(-673.61, -739.46) * mm, "end": v(-668.61, -739.46) * mm});
            skPoint(sketch, "E335.MirrorP", {"position": v(-723.61, -674.63) * mm});
            skLineSegment(sketch, "E336.MirrorCS", {"start": v(-668.61, -702.02) * mm, "end": v(-673.61, -702.02) * mm});
            skPoint(sketch, "E337.MirrorP", {"position": v(-723.61, -862.25) * mm});
            skLineSegment(sketch, "E338.MirrorCS", {"start": v(-668.61, -797.41) * mm, "end": v(-673.61, -797.41) * mm});
            skLineSegment(sketch, "E339.MirrorCS", {"start": v(-673.61, -674.63) * mm, "end": v(-668.61, -674.63) * mm});
            skLineSegment(sketch, "E340.MirrorCS", {"start": v(-696.11, -639.54) * mm, "end": v(-679.86, -639.54) * mm});
            skLineSegment(sketch, "E341.MirrorCS", {"start": v(-728.61, -902.44) * mm, "end": v(-712.36, -902.44) * mm});
            skLineSegment(sketch, "E342.MirrorCS", {"start": v(-668.61, -862.25) * mm, "end": v(-673.61, -862.25) * mm});
            skLineSegment(sketch, "E343.MirrorCS", {"start": v(-673.61, -834.86) * mm, "end": v(-668.61, -834.86) * mm});
            skLineSegment(sketch, "E344.MirrorCS", {"start": v(-673.61, -884.78) * mm, "end": v(-668.61, -884.78) * mm});
            skPoint(sketch, "E345.MirrorP", {"position": v(-733.61, -902.44) * mm});
            skPoint(sketch, "E346.MirrorP", {"position": v(-723.61, -739.46) * mm});
            skLineSegment(sketch, "E347.MirrorCS", {"start": v(-679.86, -897.44) * mm, "end": v(-712.36, -897.44) * mm});
            skPoint(sketch, "E348.MirrorP", {"position": v(-723.61, -797.41) * mm});
            skLineSegment(sketch, "E349.MirrorCS", {"start": v(-679.86, -639.54) * mm, "end": v(-712.36, -639.54) * mm});
            skPoint(sketch, "E350.MirrorP", {"position": v(-733.61, -634.44) * mm});
            skPoint(sketch, "E351.MirrorP", {"position": v(-723.61, -834.86) * mm});
            skPoint(sketch, "E352.MirrorP", {"position": v(-723.61, -702.02) * mm});
            skPoint(sketch, "E353.MirrorP", {"position": v(-723.61, -652.1) * mm});
            skPoint(sketch, "E354.MirrorP", {"position": v(-694.61, -736.59) * mm});
            skLineSegment(sketch, "E355.MirrorCS", {"start": v(-673.61, -652.1) * mm, "end": v(-673.61, -674.63) * mm});
            skLineSegment(sketch, "E356.MirrorCS", {"start": v(-728.61, -674.63) * mm, "end": v(-728.61, -652.1) * mm});
            skPoint(sketch, "E357.MirrorP", {"position": v(-668.61, -902.44) * mm});
            skLineSegment(sketch, "E358.MirrorCS", {"start": v(-728.61, -702.02) * mm, "end": v(-728.61, -739.46) * mm});
            skLineSegment(sketch, "E359.MirrorCS", {"start": v(-673.61, -862.25) * mm, "end": v(-673.61, -884.78) * mm});
            skLineSegment(sketch, "E360.MirrorCS", {"start": v(-728.61, -797.41) * mm, "end": v(-728.61, -834.86) * mm});
            skLineSegment(sketch, "E361.MirrorCS", {"start": v(-728.61, -862.25) * mm, "end": v(-728.61, -884.78) * mm});
            skLineSegment(sketch, "E362.MirrorCS", {"start": v(-679.86, -639.54) * mm, "end": v(-696.11, -639.54) * mm});
            skLineSegment(sketch, "E363.MirrorCS", {"start": v(-673.61, -702.02) * mm, "end": v(-673.61, -739.46) * mm});
            skLineSegment(sketch, "E364.MirrorCS", {"start": v(-712.36, -639.54) * mm, "end": v(-696.11, -639.54) * mm});
            skLineSegment(sketch, "E365.MirrorCS", {"start": v(-728.61, -634.44) * mm, "end": v(-712.36, -634.44) * mm});
            skPoint(sketch, "E366.MirrorP", {"position": v(-696.11, -902.44) * mm});
            skPoint(sketch, "E367.MirrorP", {"position": v(-668.61, -674.63) * mm});
            skLineSegment(sketch, "E368.MirrorCS", {"start": v(-673.61, -797.41) * mm, "end": v(-673.61, -834.86) * mm});
            skLineSegment(sketch, "E369.MirrorCS", {"start": v(-663.61, -862.25) * mm, "end": v(-668.61, -862.25) * mm});
            skLineSegment(sketch, "E370.MirrorCS", {"start": v(-663.61, -797.41) * mm, "end": v(-668.61, -797.41) * mm});
            skLineSegment(sketch, "E371.MirrorCS", {"start": v(-663.61, -634.44) * mm, "end": v(-658.61, -634.44) * mm});
            skLineSegment(sketch, "E372.MirrorCS", {"start": v(-663.61, -739.46) * mm, "end": v(-668.61, -739.46) * mm});
            skLineSegment(sketch, "E373.MirrorCS", {"start": v(-658.61, -902.44) * mm, "end": v(-663.61, -902.44) * mm});
            skLineSegment(sketch, "E374.MirrorCS", {"start": v(-663.61, -674.63) * mm, "end": v(-668.61, -674.63) * mm});
            skLineSegment(sketch, "E375.MirrorCS", {"start": v(-663.61, -884.78) * mm, "end": v(-668.61, -884.78) * mm});
            skLineSegment(sketch, "E376.MirrorCS", {"start": v(-663.61, -834.86) * mm, "end": v(-668.61, -834.86) * mm});
            skLineSegment(sketch, "E377.MirrorCS", {"start": v(-663.61, -652.1) * mm, "end": v(-668.61, -652.1) * mm});
            skLineSegment(sketch, "E378.MirrorCS", {"start": v(-663.61, -702.02) * mm, "end": v(-668.61, -702.02) * mm});
            skLineSegment(sketch, "E379.MirrorCS", {"start": v(-663.61, -862.25) * mm, "end": v(-663.61, -884.78) * mm});
            skPoint(sketch, "E380.MirrorP", {"position": v(-663.61, -639.54) * mm});
            skLineSegment(sketch, "E381.MirrorCS", {"start": v(-663.61, -739.46) * mm, "end": v(-663.61, -702.02) * mm});
            skPoint(sketch, "E382.MirrorP", {"position": v(-663.61, -897.44) * mm});
            skLineSegment(sketch, "E383.MirrorCS", {"start": v(-658.61, -634.44) * mm, "end": v(-658.61, -902.44) * mm});
            skLineSegment(sketch, "E384.MirrorCS", {"start": v(-663.61, -674.63) * mm, "end": v(-663.61, -674.63) * mm});
            skLineSegment(sketch, "E385.MirrorCS", {"start": v(-663.61, -674.63) * mm, "end": v(-663.61, -652.1) * mm});
            skLineSegment(sketch, "E386.MirrorCS", {"start": v(-663.61, -834.86) * mm, "end": v(-663.61, -797.41) * mm});
            skLineSegment(sketch, "E387.MirrorCS", {"start": v(-733.61, -902.44) * mm, "end": v(-728.61, -902.44) * mm});
            skPoint(sketch, "E388.MirrorP", {"position": v(-741.61, -718.44) * mm});
            skLineSegment(sketch, "E389.MirrorCS", {"start": v(-728.61, -674.63) * mm, "end": v(-733.61, -674.63) * mm});
            skLineSegment(sketch, "E390.MirrorCS", {"start": v(-728.61, -834.86) * mm, "end": v(-733.61, -834.86) * mm});
            skLineSegment(sketch, "E391.MirrorCS", {"start": v(-733.61, -702.02) * mm, "end": v(-733.61, -718.44) * mm});
            skLineSegment(sketch, "E392.MirrorCS", {"start": v(-728.61, -862.25) * mm, "end": v(-733.61, -862.25) * mm});
            skLineSegment(sketch, "E393.MirrorCS", {"start": v(-728.61, -652.1) * mm, "end": v(-733.61, -652.1) * mm});
            skLineSegment(sketch, "E394.MirrorCS", {"start": v(-728.61, -739.46) * mm, "end": v(-733.61, -739.46) * mm});
            skLineSegment(sketch, "E395.MirrorCS", {"start": v(-728.61, -702.02) * mm, "end": v(-733.61, -702.02) * mm});
            skLineSegment(sketch, "E396.MirrorCS", {"start": v(-728.61, -797.41) * mm, "end": v(-733.61, -797.41) * mm});
            skPoint(sketch, "E397.MirrorP", {"position": v(-728.61, -718.44) * mm});
            skLineSegment(sketch, "E398.MirrorCS", {"start": v(-728.61, -634.44) * mm, "end": v(-733.61, -634.44) * mm});
            skLineSegment(sketch, "E399.MirrorCS", {"start": v(-728.61, -884.78) * mm, "end": v(-733.61, -884.78) * mm});
            skPoint(sketch, "E400.MirrorP", {"position": v(-741.61, -634.44) * mm});
            skPoint(sketch, "E401.MirrorP", {"position": v(-728.61, -897.44) * mm});
            skPoint(sketch, "E402.MirrorP", {"position": v(-728.61, -674.63) * mm});
            skPoint(sketch, "E403.MirrorP", {"position": v(-728.61, -678.44) * mm});
            skPoint(sketch, "E404.MirrorP", {"position": v(-728.61, -702.02) * mm});
            skPoint(sketch, "E405.MirrorP", {"position": v(-728.61, -652.1) * mm});
            skPoint(sketch, "E406.MirrorP", {"position": v(-728.61, -902.44) * mm});
            skPoint(sketch, "E407.MirrorP", {"position": v(-741.61, -678.44) * mm});
            skPoint(sketch, "E408.MirrorP", {"position": v(-741.61, -748.44) * mm});
            skPoint(sketch, "E409.MirrorP", {"position": v(-728.61, -639.54) * mm});
            skPoint(sketch, "E410.MirrorP", {"position": v(-741.61, -902.44) * mm});
            skPoint(sketch, "E411.MirrorP", {"position": v(-728.61, -818.44) * mm});
            skPoint(sketch, "E412.MirrorP", {"position": v(-741.61, -834.86) * mm});
            skLineSegment(sketch, "E413.MirrorCS", {"start": v(-733.61, -797.41) * mm, "end": v(-733.61, -834.86) * mm});
            skPoint(sketch, "E414.MirrorP", {"position": v(-741.61, -818.44) * mm});
            skPoint(sketch, "E415.MirrorP", {"position": v(-731.11, -902.44) * mm});
            skPoint(sketch, "E416.MirrorP", {"position": v(-728.61, -739.46) * mm});
            skPoint(sketch, "E417.MirrorP", {"position": v(-741.61, -768.44) * mm});
            skLineSegment(sketch, "E418.MirrorCS", {"start": v(-733.61, -702.02) * mm, "end": v(-733.61, -739.46) * mm});
            skLineSegment(sketch, "E419.MirrorCS", {"start": v(-733.61, -652.1) * mm, "end": v(-733.61, -674.63) * mm});
            skPoint(sketch, "E420.MirrorP", {"position": v(-728.61, -797.41) * mm});
            skPoint(sketch, "E421.MirrorP", {"position": v(-728.61, -748.44) * mm});
            skPoint(sketch, "E422.MirrorP", {"position": v(-728.61, -634.44) * mm});
            skLineSegment(sketch, "E423.MirrorCS", {"start": v(-733.61, -862.25) * mm, "end": v(-733.61, -884.78) * mm});
            skLineSegment(sketch, "E424.MirrorCS", {"start": v(-738.61, -678.44) * mm, "end": v(-738.61, -634.44) * mm});
            skLineSegment(sketch, "E425.MirrorCS", {"start": v(-738.61, -858.44) * mm, "end": v(-738.61, -678.44) * mm});
            skLineSegment(sketch, "E426", {"start": v(-679.86, -634.44) * mm, "end": v(-663.61, -634.44) * mm});
            skLineSegment(sketch, "E427", {"start": v(-738.61, -634.44) * mm, "end": v(-733.61, -634.44) * mm});
            skLineSegment(sketch, "E428", {"start": v(-679.86, -902.44) * mm, "end": v(-663.61, -902.44) * mm});
            skLineSegment(sketch, "E429", {"start": v(-738.61, -858.44) * mm, "end": v(-738.61, -902.44) * mm});
            skLineSegment(sketch, "E430", {"start": v(-733.61, -902.44) * mm, "end": v(-738.61, -902.44) * mm});
            skPoint(sketch, "E431.MirrorCS.start.orphan", {"position": v(-696.11, -897.44) * mm});
            skPoint(sketch, "E432.start.orphan", {"position": v(-1055.11, -897.44) * mm});
            skLineSegment(sketch, "E433.MirrorCS", {"start": v(-746.61, -652.1) * mm, "end": v(-746.61, -639.44) * mm});
            skLineSegment(sketch, "E434.MirrorCS", {"start": v(-741.61, -652.1) * mm, "end": v(-746.61, -652.1) * mm});
            skLineSegment(sketch, "E435.MirrorCS", {"start": v(-741.61, -652.1) * mm, "end": v(-741.61, -674.63) * mm});
            skLineSegment(sketch, "E436.MirrorCS", {"start": v(-741.61, -674.63) * mm, "end": v(-746.61, -674.63) * mm});
            skLineSegment(sketch, "E437.MirrorCS", {"start": v(-746.61, -678.44) * mm, "end": v(-746.61, -702.02) * mm});
            skLineSegment(sketch, "E438.MirrorCS", {"start": v(-746.61, -674.63) * mm, "end": v(-746.61, -678.44) * mm});
            skLineSegment(sketch, "E439.MirrorCS", {"start": v(-741.61, -702.02) * mm, "end": v(-746.61, -702.02) * mm});
            skLineSegment(sketch, "E440.MirrorCS", {"start": v(-741.61, -718.44) * mm, "end": v(-741.61, -702.02) * mm});
            skLineSegment(sketch, "E441.MirrorCS", {"start": v(-741.61, -739.46) * mm, "end": v(-746.61, -739.46) * mm});
            skLineSegment(sketch, "E442.MirrorCS", {"start": v(-746.61, -739.46) * mm, "end": v(-746.61, -748.44) * mm});
            skLineSegment(sketch, "E443.MirrorCS", {"start": v(-746.61, -797.41) * mm, "end": v(-746.61, -788.34) * mm});
            skLineSegment(sketch, "E444.MirrorCS", {"start": v(-741.61, -797.41) * mm, "end": v(-746.61, -797.41) * mm});
            skLineSegment(sketch, "E445.MirrorCS", {"start": v(-741.61, -797.41) * mm, "end": v(-741.61, -818.44) * mm});
            skLineSegment(sketch, "E446.MirrorCS", {"start": v(-741.61, -834.86) * mm, "end": v(-746.61, -834.86) * mm});
            skLineSegment(sketch, "E447.MirrorCS", {"start": v(-746.61, -834.86) * mm, "end": v(-746.61, -858.44) * mm});
            skLineSegment(sketch, "E448.MirrorCS", {"start": v(-741.61, -862.25) * mm, "end": v(-746.61, -862.25) * mm});
            skLineSegment(sketch, "E449.MirrorCS", {"start": v(-746.61, -862.25) * mm, "end": v(-746.61, -858.44) * mm});
            skLineSegment(sketch, "E450.MirrorCS", {"start": v(-741.61, -862.25) * mm, "end": v(-741.61, -884.78) * mm});
            skLineSegment(sketch, "E451.MirrorCS", {"start": v(-741.61, -884.78) * mm, "end": v(-746.61, -884.78) * mm});
            skLineSegment(sketch, "E452.MirrorCS", {"start": v(-746.61, -884.78) * mm, "end": v(-746.61, -897.44) * mm});
            skLineSegment(sketch, "E453", {"start": v(-741.61, -818.44) * mm, "end": v(-741.61, -834.86) * mm});
            skPoint(sketch, "E454.MirrorCS.end.orphan", {"position": v(-746.61, -818.44) * mm});
            skLineSegment(sketch, "E455", {"start": v(-1164.25, -1083.61) * mm, "end": v(-1164.25, -1081.61) * mm});
            skCircle(sketch, "E456", {"center": v(-1164.25, -1081.61) * mm, "radius": 2 * mm});
            skCircle(sketch, "E457", {"center": v(-1164.25, -1329.11) * mm, "radius": 2 * mm});
            skCircle(sketch, "E458", {"center": v(-1251.75, -1117.86) * mm, "radius": 2 * mm});
            skCircle(sketch, "E459.MirrorC", {"center": v(-1251.75, -1292.87) * mm, "radius": 2 * mm});
            skPoint(sketch, "E460.orphan", {"position": v(-1164.25, -1205.36) * mm});
            skLineSegment(sketch, "E461.MirrorCS", {"start": v(-1293.25, -1334.36) * mm, "end": v(-1228.75, -1334.36) * mm});
            skLineSegment(sketch, "E462.MirrorCS", {"start": v(-1228.75, -1339.36) * mm, "end": v(-1228.75, -1334.36) * mm});
            skLineSegment(sketch, "E463.MirrorCS", {"start": v(-1228.75, -1339.36) * mm, "end": v(-1196.5, -1339.36) * mm});
            skLineSegment(sketch, "E464.MirrorCS", {"start": v(-1196.5, -1339.36) * mm, "end": v(-1196.5, -1334.36) * mm});
            skPoint(sketch, "E465.orphan", {"position": v(-1164.25, -1173.51) * mm});
            skLineSegment(sketch, "E466", {"start": v(-1293.25, -1111.55) * mm, "end": v(-1293.25, -1138.94) * mm});
            skLineSegment(sketch, "E467", {"start": v(-1293.25, -1138.94) * mm, "end": v(-1298.25, -1138.94) * mm});
            skLineSegment(sketch, "E468", {"start": v(-1298.25, -1138.94) * mm, "end": v(-1298.25, -1176.39) * mm});
            skLineSegment(sketch, "E469", {"start": v(-1298.25, -1176.39) * mm, "end": v(-1293.25, -1176.39) * mm});
            skLineSegment(sketch, "E470", {"start": v(-1293.25, -1176.39) * mm, "end": v(-1293.25, -1234.34) * mm});
            skLineSegment(sketch, "E471", {"start": v(-1293.25, -1234.34) * mm, "end": v(-1298.25, -1234.34) * mm});
            skLineSegment(sketch, "E472", {"start": v(-1298.25, -1234.34) * mm, "end": v(-1298.25, -1271.78) * mm});
            skLineSegment(sketch, "E473", {"start": v(-1298.25, -1271.78) * mm, "end": v(-1293.25, -1271.78) * mm});
            skLineSegment(sketch, "E474", {"start": v(-1293.25, -1271.78) * mm, "end": v(-1293.25, -1299.17) * mm});
            skLineSegment(sketch, "E475", {"start": v(-1293.25, -1299.17) * mm, "end": v(-1298.25, -1299.17) * mm});
            skLineSegment(sketch, "E476", {"start": v(-1298.25, -1299.17) * mm, "end": v(-1298.25, -1321.7) * mm});
            skLineSegment(sketch, "E477", {"start": v(-1298.25, -1321.7) * mm, "end": v(-1293.25, -1321.7) * mm});
            skLineSegment(sketch, "E478", {"start": v(-1293.25, -1321.7) * mm, "end": v(-1293.25, -1334.36) * mm});
            skLineSegment(sketch, "E479", {"start": v(-1164.25, -1205.36) * mm, "end": v(-1164.25, -1185.71) * mm});
            skLineSegment(sketch, "E480.MirrorCS", {"start": v(-1035.25, -1111.55) * mm, "end": v(-1035.25, -1138.94) * mm});
            skLineSegment(sketch, "E481.MirrorCS", {"start": v(-1035.25, -1138.94) * mm, "end": v(-1030.25, -1138.94) * mm});
            skLineSegment(sketch, "E482.MirrorCS", {"start": v(-1030.25, -1138.94) * mm, "end": v(-1030.25, -1176.39) * mm});
            skLineSegment(sketch, "E483.MirrorCS", {"start": v(-1030.25, -1176.39) * mm, "end": v(-1035.25, -1176.39) * mm});
            skLineSegment(sketch, "E484.MirrorCS", {"start": v(-1035.25, -1176.39) * mm, "end": v(-1035.25, -1234.34) * mm});
            skLineSegment(sketch, "E485.MirrorCS", {"start": v(-1035.25, -1234.34) * mm, "end": v(-1030.25, -1234.34) * mm});
            skLineSegment(sketch, "E486.MirrorCS", {"start": v(-1030.25, -1234.34) * mm, "end": v(-1030.25, -1271.78) * mm});
            skLineSegment(sketch, "E487.MirrorCS", {"start": v(-1030.25, -1271.78) * mm, "end": v(-1035.25, -1271.78) * mm});
            skLineSegment(sketch, "E488.MirrorCS", {"start": v(-1035.25, -1271.78) * mm, "end": v(-1035.25, -1299.17) * mm});
            skLineSegment(sketch, "E489.MirrorCS", {"start": v(-1035.25, -1299.17) * mm, "end": v(-1030.25, -1299.17) * mm});
            skLineSegment(sketch, "E490.MirrorCS", {"start": v(-1030.25, -1299.17) * mm, "end": v(-1030.25, -1321.7) * mm});
            skLineSegment(sketch, "E491.MirrorCS", {"start": v(-1030.25, -1321.7) * mm, "end": v(-1035.25, -1321.7) * mm});
            skLineSegment(sketch, "E492.MirrorCS", {"start": v(-1035.25, -1334.36) * mm, "end": v(-1099.75, -1334.36) * mm});
            skLineSegment(sketch, "E493.MirrorCS", {"start": v(-1099.75, -1339.36) * mm, "end": v(-1099.75, -1334.36) * mm});
            skLineSegment(sketch, "E494.MirrorCS", {"start": v(-1099.75, -1339.36) * mm, "end": v(-1132, -1339.36) * mm});
            skLineSegment(sketch, "E495.MirrorCS", {"start": v(-1132, -1339.36) * mm, "end": v(-1132, -1334.36) * mm});
            skLineSegment(sketch, "E496", {"start": v(-1196.5, -1334.36) * mm, "end": v(-1132, -1334.36) * mm});
            skLineSegment(sketch, "E497", {"start": v(-1035.25, -1321.7) * mm, "end": v(-1035.25, -1334.36) * mm});
            skLineSegment(sketch, "E498", {"start": v(-1164.25, -1205.36) * mm, "end": v(-1227.77, -1205.36) * mm});
            skLineSegment(sketch, "E499.MirrorCS", {"start": v(-1298.25, -1089.02) * mm, "end": v(-1293.25, -1089.02) * mm});
            skLineSegment(sketch, "E500.MirrorCS", {"start": v(-1293.25, -1111.55) * mm, "end": v(-1298.25, -1111.55) * mm});
            skLineSegment(sketch, "E501.MirrorCS", {"start": v(-1293.25, -1138.94) * mm, "end": v(-1293.25, -1111.55) * mm});
            skLineSegment(sketch, "E502.MirrorCS", {"start": v(-1293.25, -1089.02) * mm, "end": v(-1293.25, -1076.36) * mm});
            skLineSegment(sketch, "E503.MirrorCS", {"start": v(-1293.25, -1076.36) * mm, "end": v(-1228.75, -1076.36) * mm});
            skLineSegment(sketch, "E504.MirrorCS", {"start": v(-1228.75, -1071.36) * mm, "end": v(-1228.75, -1076.36) * mm});
            skLineSegment(sketch, "E505.MirrorCS", {"start": v(-1228.75, -1071.36) * mm, "end": v(-1196.5, -1071.36) * mm});
            skLineSegment(sketch, "E506.MirrorCS", {"start": v(-1099.75, -1071.36) * mm, "end": v(-1132, -1071.36) * mm});
            skLineSegment(sketch, "E507.MirrorCS", {"start": v(-1099.75, -1071.36) * mm, "end": v(-1099.75, -1076.36) * mm});
            skLineSegment(sketch, "E508.MirrorCS", {"start": v(-1035.25, -1076.36) * mm, "end": v(-1099.75, -1076.36) * mm});
            skLineSegment(sketch, "E509.MirrorCS", {"start": v(-1035.25, -1089.02) * mm, "end": v(-1035.25, -1076.36) * mm});
            skLineSegment(sketch, "E510.MirrorCS", {"start": v(-1030.25, -1089.02) * mm, "end": v(-1035.25, -1089.02) * mm});
            skLineSegment(sketch, "E511.MirrorCS", {"start": v(-1030.25, -1111.55) * mm, "end": v(-1030.25, -1089.02) * mm});
            skLineSegment(sketch, "E512.MirrorCS", {"start": v(-1035.25, -1111.55) * mm, "end": v(-1030.25, -1111.55) * mm});
            skLineSegment(sketch, "E513.MirrorCS", {"start": v(-1035.25, -1138.94) * mm, "end": v(-1035.25, -1111.55) * mm});
            skLineSegment(sketch, "E514.MirrorCS", {"start": v(-1030.25, -1138.94) * mm, "end": v(-1035.25, -1138.94) * mm});
            skLineSegment(sketch, "E515.MirrorCS", {"start": v(-1030.25, -1176.39) * mm, "end": v(-1030.25, -1138.94) * mm});
            skLineSegment(sketch, "E516.MirrorCS", {"start": v(-1196.5, -1076.36) * mm, "end": v(-1132, -1076.36) * mm});
            skLineSegment(sketch, "E517.MirrorCS", {"start": v(-1196.5, -1071.36) * mm, "end": v(-1196.5, -1076.36) * mm});
            skLineSegment(sketch, "E518.MirrorCS", {"start": v(-1132, -1071.36) * mm, "end": v(-1132, -1076.36) * mm});
            skLineSegment(sketch, "E519.MirrorCS", {"start": v(-1298.25, -1111.55) * mm, "end": v(-1298.25, -1089.02) * mm});
            skCircle(sketch, "E520.MirrorC", {"center": v(-1076.74, -1117.86) * mm, "radius": 2 * mm});
            skCircle(sketch, "E521.MirrorC", {"center": v(-1076.74, -1292.87) * mm, "radius": 2 * mm});
            skLineSegment(sketch, "E522", {"start": v(-1164.25, -1205.36) * mm, "end": v(-1260.14, -1205.36) * mm});
            skCircle(sketch, "E523", {"center": v(-1288, -1205.36) * mm, "radius": 2 * mm});
            skCircle(sketch, "E524", {"center": v(-1164.25, -1205.36) * mm, "radius": 118.66 * mm});
            skPoint(sketch, "E525.trimOffspring.end.orphan", {"position": v(-1293.25, -1205.36) * mm});
            skCircle(sketch, "E526.MirrorC", {"center": v(-1040.5, -1205.36) * mm, "radius": 2 * mm});
            skLineSegment(sketch, "E527", {"start": v(-940.11, -560.24) * mm, "end": v(-940.11, -565.24) * mm});
            skLineSegment(sketch, "E528", {"start": v(-940.11, -565.24) * mm, "end": v(-907.86, -565.24) * mm});
            skLineSegment(sketch, "E529", {"start": v(-907.86, -565.24) * mm, "end": v(-907.86, -560.24) * mm});
            skLineSegment(sketch, "E530", {"start": v(-843.36, -560.24) * mm, "end": v(-843.36, -565.24) * mm});
            skLineSegment(sketch, "E531", {"start": v(-843.36, -565.24) * mm, "end": v(-811.11, -565.24) * mm});
            skLineSegment(sketch, "E532", {"start": v(-811.11, -565.24) * mm, "end": v(-811.11, -560.24) * mm});
            skLineSegment(sketch, "E533.MirrorCS", {"start": v(-940.11, -976.63) * mm, "end": v(-940.11, -971.63) * mm});
            skLineSegment(sketch, "E534.MirrorCS", {"start": v(-940.11, -971.63) * mm, "end": v(-907.86, -971.63) * mm});
            skLineSegment(sketch, "E535.MirrorCS", {"start": v(-907.86, -971.63) * mm, "end": v(-907.86, -976.63) * mm});
            skLineSegment(sketch, "E536.MirrorCS", {"start": v(-843.36, -976.63) * mm, "end": v(-843.36, -971.63) * mm});
            skLineSegment(sketch, "E537.MirrorCS", {"start": v(-843.36, -971.63) * mm, "end": v(-811.11, -971.63) * mm});
            skLineSegment(sketch, "E538.MirrorCS", {"start": v(-811.11, -971.63) * mm, "end": v(-811.11, -976.63) * mm});
            skLineSegment(sketch, "E539", {"start": v(-844.99, -768.44) * mm, "end": v(-795.61, -768.44) * mm});
            skLineSegment(sketch, "E540", {"start": v(-875.61, -768.44) * mm, "end": v(-875.61, -848.44) * mm});
            skLineSegment(sketch, "E541", {"start": v(-875.61, -848.44) * mm, "end": v(-875.61, -768.44) * mm});
            skLineSegment(sketch, "E542.top", {"start": v(-875.61, -768.44) * mm, "end": v(-795.61, -768.44) * mm});
            skLineSegment(sketch, "E543", {"start": v(-875.61, -768.44) * mm, "end": v(-955.61, -768.44) * mm});
            skLineSegment(sketch, "E544", {"start": v(-875.61, -768.44) * mm, "end": v(-875.61, -688.44) * mm});
            skLineSegment(sketch, "E545.left", {"start": v(-875.61, -688.44) * mm, "end": v(-875.61, -768.44) * mm});
            skLineSegment(sketch, "E546", {"start": v(-960.61, -768.44) * mm, "end": v(-960.61, -748.44) * mm});
            skLineSegment(sketch, "E547", {"start": v(-960.61, -748.44) * mm, "end": v(-965.61, -748.44) * mm});
            skLineSegment(sketch, "E548.bottom", {"start": v(-965.61, -702.44) * mm, "end": v(-960.61, -702.44) * mm});
            skLineSegment(sketch, "E548.top", {"start": v(-965.61, -728.44) * mm, "end": v(-960.61, -728.44) * mm});
            skLineSegment(sketch, "E548.left", {"start": v(-965.61, -702.44) * mm, "end": v(-965.61, -728.44) * mm});
            skLineSegment(sketch, "E548.right", {"start": v(-960.61, -702.44) * mm, "end": v(-960.61, -728.44) * mm});
            skLineSegment(sketch, "E549.MirrorCS", {"start": v(-960.61, -788.44) * mm, "end": v(-965.61, -788.44) * mm});
            skLineSegment(sketch, "E550.MirrorCS", {"start": v(-965.61, -808.44) * mm, "end": v(-960.61, -808.44) * mm});
            skLineSegment(sketch, "E551.MirrorCS", {"start": v(-965.61, -834.44) * mm, "end": v(-960.61, -834.44) * mm});
            skLineSegment(sketch, "E552.trimOffspring", {"start": v(-965.61, -808.44) * mm, "end": v(-965.61, -834.44) * mm});
            skLineSegment(sketch, "E553", {"start": v(-965.61, -748.44) * mm, "end": v(-965.61, -788.44) * mm});
            skLineSegment(sketch, "E554.trimOffspring", {"start": v(-960.61, -808.44) * mm, "end": v(-960.61, -834.44) * mm});
            skLineSegment(sketch, "E555", {"start": v(-960.61, -768.44) * mm, "end": v(-960.61, -788.44) * mm});
            skLineSegment(sketch, "E556.MirrorCS", {"start": v(-790.61, -748.44) * mm, "end": v(-785.61, -748.44) * mm});
            skLineSegment(sketch, "E557.MirrorCS", {"start": v(-785.61, -702.44) * mm, "end": v(-790.61, -702.44) * mm});
            skLineSegment(sketch, "E558.MirrorCS", {"start": v(-785.61, -728.44) * mm, "end": v(-790.61, -728.44) * mm});
            skLineSegment(sketch, "E559.MirrorCS", {"start": v(-790.61, -788.44) * mm, "end": v(-785.61, -788.44) * mm});
            skLineSegment(sketch, "E560.MirrorCS", {"start": v(-785.61, -808.44) * mm, "end": v(-790.61, -808.44) * mm});
            skLineSegment(sketch, "E561.MirrorCS", {"start": v(-785.61, -834.44) * mm, "end": v(-790.61, -834.44) * mm});
            skLineSegment(sketch, "E562.MirrorCS", {"start": v(-785.61, -768.44) * mm, "end": v(-790.61, -768.44) * mm});
            skLineSegment(sketch, "E563.MirrorCS", {"start": v(-790.61, -808.44) * mm, "end": v(-790.61, -834.44) * mm});
            skLineSegment(sketch, "E564.MirrorCS", {"start": v(-790.61, -768.44) * mm, "end": v(-790.61, -748.44) * mm});
            skLineSegment(sketch, "E565.MirrorCS", {"start": v(-790.61, -768.44) * mm, "end": v(-790.61, -788.44) * mm});
            skLineSegment(sketch, "E566.MirrorCS", {"start": v(-785.61, -702.44) * mm, "end": v(-785.61, -728.44) * mm});
            skLineSegment(sketch, "E567.MirrorCS", {"start": v(-790.61, -702.44) * mm, "end": v(-790.61, -728.44) * mm});
            skLineSegment(sketch, "E568.MirrorCS", {"start": v(-785.61, -808.44) * mm, "end": v(-785.61, -834.44) * mm});
            skLineSegment(sketch, "E569.MirrorCS", {"start": v(-785.61, -748.44) * mm, "end": v(-785.61, -788.44) * mm});
            skLineSegment(sketch, "E570.bottom", {"start": v(-941.61, -853.44) * mm, "end": v(-915.61, -853.44) * mm});
            skLineSegment(sketch, "E570.top", {"start": v(-941.61, -858.44) * mm, "end": v(-915.61, -858.44) * mm});
            skLineSegment(sketch, "E570.left", {"start": v(-941.61, -853.44) * mm, "end": v(-941.61, -858.44) * mm});
            skLineSegment(sketch, "E570.right", {"start": v(-915.61, -853.44) * mm, "end": v(-915.61, -858.44) * mm});
            skLineSegment(sketch, "E571", {"start": v(-895.61, -853.44) * mm, "end": v(-895.61, -858.44) * mm});
            skLineSegment(sketch, "E572", {"start": v(-895.61, -858.44) * mm, "end": v(-875.61, -858.44) * mm});
            skLineSegment(sketch, "E573.MirrorCS", {"start": v(-855.61, -858.44) * mm, "end": v(-875.61, -858.44) * mm});
            skLineSegment(sketch, "E574.MirrorCS", {"start": v(-855.61, -853.44) * mm, "end": v(-855.61, -858.44) * mm});
            skLineSegment(sketch, "E575.MirrorCS", {"start": v(-835.61, -853.44) * mm, "end": v(-835.61, -858.44) * mm});
            skLineSegment(sketch, "E576.MirrorCS", {"start": v(-809.61, -858.44) * mm, "end": v(-835.61, -858.44) * mm});
            skLineSegment(sketch, "E577.MirrorCS", {"start": v(-809.61, -853.44) * mm, "end": v(-809.61, -858.44) * mm});
            skLineSegment(sketch, "E578.trimOffspring", {"start": v(-855.61, -853.44) * mm, "end": v(-895.61, -853.44) * mm});
            skLineSegment(sketch, "E579", {"start": v(-835.61, -853.44) * mm, "end": v(-809.61, -853.44) * mm});
            skPoint(sketch, "E580.start.orphan", {"position": v(-965.61, -768.44) * mm});
            skPoint(sketch, "E581.end.orphan", {"position": v(-875.61, -853.44) * mm});
            skLineSegment(sketch, "E582", {"start": v(-897.61, -666.44) * mm, "end": v(-875.61, -666.44) * mm});
            skLineSegment(sketch, "E583", {"start": v(-905.61, -678.44) * mm, "end": v(-905.61, -683.44) * mm});
            skLineSegment(sketch, "E584", {"start": v(-920.61, -678.44) * mm, "end": v(-920.61, -683.44) * mm});
            skLineSegment(sketch, "E585", {"start": v(-935.61, -678.44) * mm, "end": v(-935.61, -683.44) * mm});
            skLineSegment(sketch, "E586", {"start": v(-950.61, -678.44) * mm, "end": v(-950.61, -683.44) * mm});
            skPoint(sketch, "E587.start.orphan", {"position": v(-935, -683.44) * mm});
            skLineSegment(sketch, "E588", {"start": v(-905.61, -678.44) * mm, "end": v(-920.61, -678.44) * mm});
            skPoint(sketch, "E589.start.orphan", {"position": v(-909.4, -678.44) * mm});
            skPoint(sketch, "E590.orphan", {"position": v(-960.61, -683.44) * mm});
            skPoint(sketch, "E591.left.start.orphan", {"position": v(-909.4, -683.44) * mm});
            skLineSegment(sketch, "E592.bottom", {"start": v(-950.61, -678.44) * mm, "end": v(-935.61, -678.44) * mm});
            skLineSegment(sketch, "E592.top", {"start": v(-950.61, -683.44) * mm, "end": v(-935.61, -683.44) * mm});
            skLineSegment(sketch, "E593.bottom", {"start": v(-920.61, -678.44) * mm, "end": v(-905.61, -678.44) * mm});
            skLineSegment(sketch, "E593.top", {"start": v(-920.61, -683.44) * mm, "end": v(-905.61, -683.44) * mm});
            skLineSegment(sketch, "E594.MirrorCS", {"start": v(-800.61, -678.44) * mm, "end": v(-800.61, -683.44) * mm});
            skLineSegment(sketch, "E595.MirrorCS", {"start": v(-815.61, -678.44) * mm, "end": v(-815.61, -683.44) * mm});
            skLineSegment(sketch, "E596.MirrorCS", {"start": v(-830.61, -678.44) * mm, "end": v(-830.61, -683.44) * mm});
            skLineSegment(sketch, "E597.MirrorCS", {"start": v(-845.61, -678.44) * mm, "end": v(-845.61, -683.44) * mm});
            skLineSegment(sketch, "E598.MirrorCS", {"start": v(-845.61, -678.44) * mm, "end": v(-830.61, -678.44) * mm});
            skPoint(sketch, "E599.MirrorP", {"position": v(-816.22, -683.44) * mm});
            skLineSegment(sketch, "E600.MirrorCS", {"start": v(-830.61, -683.44) * mm, "end": v(-845.61, -683.44) * mm});
            skLineSegment(sketch, "E601.MirrorCS", {"start": v(-830.61, -678.44) * mm, "end": v(-845.61, -678.44) * mm});
            skLineSegment(sketch, "E602.MirrorCS", {"start": v(-800.61, -683.44) * mm, "end": v(-815.61, -683.44) * mm});
            skLineSegment(sketch, "E603.MirrorCS", {"start": v(-800.61, -678.44) * mm, "end": v(-815.61, -678.44) * mm});
            skPoint(sketch, "E604.MirrorP", {"position": v(-790.61, -683.44) * mm});
            skLineSegment(sketch, "E605", {"start": v(-890.61, -656.44) * mm, "end": v(-880.61, -656.44) * mm});
            skLineSegment(sketch, "E606.bottom", {"start": v(-880.61, -661.44) * mm, "end": v(-890.61, -661.44) * mm});
            skLineSegment(sketch, "E606.top", {"start": v(-880.61, -656.44) * mm, "end": v(-890.61, -656.44) * mm});
            skLineSegment(sketch, "E606.left", {"start": v(-880.61, -661.44) * mm, "end": v(-880.61, -656.44) * mm});
            skLineSegment(sketch, "E606.right", {"start": v(-890.61, -661.44) * mm, "end": v(-890.61, -656.44) * mm});
            skLineSegment(sketch, "E607.MirrorCS", {"start": v(-870.61, -661.44) * mm, "end": v(-870.61, -656.44) * mm});
            skLineSegment(sketch, "E608.MirrorCS", {"start": v(-860.61, -661.44) * mm, "end": v(-860.61, -656.44) * mm});
            skPoint(sketch, "E609.orphan", {"position": v(-853.61, -656.44) * mm});
            skLineSegment(sketch, "E610.trimOffspring", {"start": v(-870.61, -656.44) * mm, "end": v(-860.61, -656.44) * mm});
            skPoint(sketch, "E611.start.orphan", {"position": v(-853.61, -661.44) * mm});
            skLineSegment(sketch, "E612", {"start": v(-870.61, -661.44) * mm, "end": v(-860.61, -661.44) * mm});
            skArc(sketch, "E613", {"start": v(-223.39, -495.23) * mm, "mid": v(-201.39, -652.15) * mm, "end": v(-179.39, -495.23) * mm});
            skLineSegment(sketch, "E614", {"start": v(-201.39, -470.15) * mm, "end": v(-196.5, -470.15) * mm});
            skLineSegment(sketch, "E615", {"start": v(-201.39, -470.15) * mm, "end": v(-179.39, -470.15) * mm});
            skLineSegment(sketch, "E616", {"start": v(-179.39, -470.15) * mm, "end": v(-179.39, -495.23) * mm});
            skLineSegment(sketch, "E617", {"start": v(-223.39, -470.15) * mm, "end": v(-223.39, -495.23) * mm});
            skPoint(sketch, "E618.end.orphan", {"position": v(-201.39, -540.3) * mm});
            skPoint(sketch, "E619.end.orphan", {"position": v(-237.62, -572.13) * mm});
            skLineSegment(sketch, "E620", {"start": v(-201.39, -572.15) * mm, "end": v(-201.39, -540.3) * mm});
            skCircle(sketch, "E621", {"center": v(-266.4, -641.25) * mm, "radius": 7.1 * mm});
            skLineSegment(sketch, "E622", {"start": v(-201.39, -572.15) * mm, "end": v(-170.76, -572.15) * mm});
            skLineSegment(sketch, "E623", {"start": v(-170.76, -572.15) * mm, "end": v(-121.39, -572.15) * mm});
            skLineSegment(sketch, "E624", {"start": v(-201.39, -572.15) * mm, "end": v(-201.39, -652.15) * mm});
            skLineSegment(sketch, "E625", {"start": v(-201.39, -652.15) * mm, "end": v(-201.39, -572.15) * mm});
            skLineSegment(sketch, "E626.top", {"start": v(-201.39, -572.15) * mm, "end": v(-121.39, -572.15) * mm});
            skLineSegment(sketch, "E627", {"start": v(-201.39, -572.15) * mm, "end": v(-281.39, -572.15) * mm});
            skLineSegment(sketch, "E628", {"start": v(-201.39, -572.15) * mm, "end": v(-201.39, -492.15) * mm});
            skLineSegment(sketch, "E629.left", {"start": v(-201.39, -492.15) * mm, "end": v(-201.39, -572.15) * mm});
            skLineSegment(sketch, "E630.MirrorCS", {"start": v(-116.39, -552.17) * mm, "end": v(-111.39, -552.17) * mm});
            skLineSegment(sketch, "E631.MirrorCS", {"start": v(-111.39, -506.17) * mm, "end": v(-116.39, -506.17) * mm});
            skLineSegment(sketch, "E632.MirrorCS", {"start": v(-111.39, -532.17) * mm, "end": v(-116.39, -532.17) * mm});
            skLineSegment(sketch, "E633.MirrorCS", {"start": v(-116.39, -592.13) * mm, "end": v(-111.39, -592.13) * mm});
            skLineSegment(sketch, "E634.MirrorCS", {"start": v(-111.39, -612.13) * mm, "end": v(-116.39, -612.13) * mm});
            skLineSegment(sketch, "E635.MirrorCS", {"start": v(-111.39, -638.13) * mm, "end": v(-116.39, -638.13) * mm});
            skLineSegment(sketch, "E636.MirrorCS", {"start": v(-111.39, -572.17) * mm, "end": v(-116.39, -572.17) * mm});
            skLineSegment(sketch, "E637.MirrorCS", {"start": v(-116.39, -612.13) * mm, "end": v(-116.39, -638.13) * mm});
            skLineSegment(sketch, "E638.MirrorCS", {"start": v(-116.39, -572.17) * mm, "end": v(-116.39, -552.17) * mm});
            skLineSegment(sketch, "E639.MirrorCS", {"start": v(-116.39, -572.17) * mm, "end": v(-116.39, -592.13) * mm});
            skLineSegment(sketch, "E640.MirrorCS", {"start": v(-111.39, -506.17) * mm, "end": v(-111.39, -532.17) * mm});
            skLineSegment(sketch, "E641.MirrorCS", {"start": v(-116.39, -506.17) * mm, "end": v(-116.39, -532.17) * mm});
            skLineSegment(sketch, "E642.MirrorCS", {"start": v(-111.39, -612.13) * mm, "end": v(-111.39, -638.13) * mm});
            skLineSegment(sketch, "E643.MirrorCS", {"start": v(-111.39, -552.17) * mm, "end": v(-111.39, -592.13) * mm});
            skLineSegment(sketch, "E644", {"start": v(-223.39, -470.15) * mm, "end": v(-201.39, -470.15) * mm});
            skPoint(sketch, "E645.start.orphan", {"position": v(-261.39, -487.13) * mm});
            skPoint(sketch, "E646.start.orphan", {"position": v(-235.17, -482.13) * mm});
            skPoint(sketch, "E647.left.start.orphan", {"position": v(-235.17, -487.13) * mm});
            skLineSegment(sketch, "E648.bottom", {"start": v(-276.39, -482.13) * mm, "end": v(-271.39, -482.13) * mm});
            skLineSegment(sketch, "E649.top", {"start": v(-246.39, -487.13) * mm, "end": v(-241.39, -487.13) * mm});
            skLineSegment(sketch, "E650", {"start": v(-206.39, -460.15) * mm, "end": v(-186.39, -460.15) * mm});
            skLineSegment(sketch, "E651.bottom", {"start": v(-186.39, -465.15) * mm, "end": v(-206.39, -465.15) * mm});
            skLineSegment(sketch, "E651.top", {"start": v(-186.39, -460.15) * mm, "end": v(-206.39, -460.15) * mm});
            skLineSegment(sketch, "E651.left", {"start": v(-206.39, -465.15) * mm, "end": v(-206.39, -460.15) * mm});
            skLineSegment(sketch, "E651.right", {"start": v(-186.39, -465.15) * mm, "end": v(-186.39, -460.15) * mm});
            skLineSegment(sketch, "E652.MirrorCS", {"start": v(-196.39, -465.15) * mm, "end": v(-196.39, -460.15) * mm});
            skLineSegment(sketch, "E653.MirrorCS", {"start": v(-216.39, -465.15) * mm, "end": v(-216.39, -460.15) * mm});
            skLineSegment(sketch, "E654.trimOffspring", {"start": v(-216.39, -460.15) * mm, "end": v(-196.39, -460.15) * mm});
            skLineSegment(sketch, "E655", {"start": v(-216.39, -465.15) * mm, "end": v(-196.39, -465.15) * mm});
            skLineSegment(sketch, "E656", {"start": v(-284.39, -461) * mm, "end": v(-286.39, -461) * mm});
            skLineSegment(sketch, "E657", {"start": v(-276.39, -466) * mm, "end": v(-271.39, -466) * mm});
            skLineSegment(sketch, "E658", {"start": v(-246.39, -466) * mm, "end": v(-241.39, -466) * mm});
            skLineSegment(sketch, "E659", {"start": v(-225.37, -461.03) * mm, "end": v(-225.37, -371.03) * mm});
            skPoint(sketch, "E660.orphan", {"position": v(-286.39, -281.03) * mm});
            skLineSegment(sketch, "E661", {"start": v(-223.39, -359.79) * mm, "end": v(-216.39, -359.79) * mm});
            skLineSegment(sketch, "E662", {"start": v(-201.32, -449.79) * mm, "end": v(-206.39, -449.79) * mm});
            skLineSegment(sketch, "E663", {"start": v(-206.39, -449.79) * mm, "end": v(-206.39, -454.79) * mm});
            skLineSegment(sketch, "E664", {"start": v(-186.39, -454.79) * mm, "end": v(-196.39, -454.79) * mm});
            skLineSegment(sketch, "E665", {"start": v(-186.39, -454.79) * mm, "end": v(-186.39, -449.79) * mm});
            skLineSegment(sketch, "E666.MirrorCS", {"start": v(-177.4, -461.03) * mm, "end": v(-177.4, -371.03) * mm});
            skLineSegment(sketch, "E667.MirrorCS", {"start": v(-216.39, -454.79) * mm, "end": v(-206.39, -454.79) * mm});
            skLineSegment(sketch, "E668.MirrorCS", {"start": v(-196.39, -449.79) * mm, "end": v(-196.39, -454.79) * mm});
            skLineSegment(sketch, "E669.MirrorCS", {"start": v(-201.45, -449.79) * mm, "end": v(-196.39, -449.79) * mm});
            skLineSegment(sketch, "E670.MirrorCS", {"start": v(-201.32, -449.79) * mm, "end": v(-196.39, -449.79) * mm});
            skLineSegment(sketch, "E671.MirrorCS", {"start": v(-179.39, -449.79) * mm, "end": v(-179.39, -359.79) * mm});
            skLineSegment(sketch, "E672.MirrorCS", {"start": v(-179.39, -359.79) * mm, "end": v(-186.39, -359.79) * mm});
            skLineSegment(sketch, "E673.MirrorCS", {"start": v(-104.64, -506.13) * mm, "end": v(-104.64, -482.13) * mm});
            skLineSegment(sketch, "E674.MirrorCS", {"start": v(-109.64, -506.17) * mm, "end": v(-104.64, -506.13) * mm});
            skLineSegment(sketch, "E675.MirrorCS", {"start": v(-109.64, -506.17) * mm, "end": v(-109.64, -532.17) * mm});
            skLineSegment(sketch, "E676.MirrorCS", {"start": v(-109.64, -532.17) * mm, "end": v(-104.64, -532.17) * mm});
            skLineSegment(sketch, "E677.MirrorCS", {"start": v(-104.64, -532.17) * mm, "end": v(-104.64, -552.17) * mm});
            skLineSegment(sketch, "E678.MirrorCS", {"start": v(-104.64, -552.17) * mm, "end": v(-109.64, -552.17) * mm});
            skLineSegment(sketch, "E679.MirrorCS", {"start": v(-109.64, -552.13) * mm, "end": v(-109.64, -592.13) * mm});
            skLineSegment(sketch, "E680.MirrorCS", {"start": v(-109.64, -592.13) * mm, "end": v(-104.64, -592.13) * mm});
            skLineSegment(sketch, "E681.MirrorCS", {"start": v(-104.64, -592.13) * mm, "end": v(-104.64, -612.13) * mm});
            skLineSegment(sketch, "E682.MirrorCS", {"start": v(-104.64, -612.13) * mm, "end": v(-109.64, -612.13) * mm});
            skLineSegment(sketch, "E683.MirrorCS", {"start": v(-109.64, -612.13) * mm, "end": v(-109.64, -638.13) * mm});
            skLineSegment(sketch, "E684.MirrorCS", {"start": v(-109.64, -638.13) * mm, "end": v(-104.64, -638.13) * mm});
            skLineSegment(sketch, "E685.MirrorCS", {"start": v(-104.64, -638.13) * mm, "end": v(-104.64, -662.13) * mm});
            skLineSegment(sketch, "E686", {"start": v(90.34, -674.04) * mm, "end": v(90.34, -431.72) * mm});
            skLineSegment(sketch, "E687.top", {"start": v(-593, -35.7) * mm, "end": v(-823, -35.7) * mm});
            skLineSegment(sketch, "E687.right", {"start": v(-823, -305.7) * mm, "end": v(-823, -35.7) * mm});
            skLineSegment(sketch, "E688", {"start": v(-593, -35.7) * mm, "end": v(-593, -210.7) * mm});
            skLineSegment(sketch, "E689", {"start": v(-593, -35.7) * mm, "end": v(-593, -305.7) * mm});
            skLineSegment(sketch, "E690", {"start": v(-593, -305.7) * mm, "end": v(-608, -305.7) * mm});
            skLineSegment(sketch, "E691", {"start": v(-823, -305.7) * mm, "end": v(-808, -305.7) * mm});
            skLineSegment(sketch, "E692", {"start": v(-808, -305.7) * mm, "end": v(-808, -385.7) * mm});
            skLineSegment(sketch, "E693", {"start": v(-608, -305.7) * mm, "end": v(-608, -385.7) * mm});
            skLineSegment(sketch, "E694.trimOffspring", {"start": v(-808, -305.7) * mm, "end": v(-823, -305.7) * mm});
            skPoint(sketch, "E695.orphan", {"position": v(-593, -385.7) * mm});
            skLineSegment(sketch, "E696", {"start": v(-808, -385.7) * mm, "end": v(-608, -385.7) * mm});
            skCircle(sketch, "E697", {"center": v(-201.39, -572.15) * mm, "radius": 70 * mm});
            skLineSegment(sketch, "E698", {"start": v(-131.39, -572.15) * mm, "end": v(-126.39, -572.15) * mm});
            skPoint(sketch, "E699.MirrorCS.start.orphan", {"position": v(-104.64, -662.13) * mm});
            skPoint(sketch, "E700.MirrorCS.start.orphan", {"position": v(-104.64, -482.13) * mm});
            skLineSegment(sketch, "E701", {"start": v(-104.64, -662.13) * mm, "end": v(-104.33, -662.13) * mm});
            skLineSegment(sketch, "E702.trimOffspring", {"start": v(-216.39, -449.79) * mm, "end": v(-223.39, -449.79) * mm});
            skLineSegment(sketch, "E703.trimOffspring", {"start": v(-186.39, -449.79) * mm, "end": v(-179.39, -449.79) * mm});
            skPoint(sketch, "E704.orphan", {"position": v(-216.39, -449.79) * mm});
            skPoint(sketch, "E705.orphan", {"position": v(-196.39, -454.79) * mm});
            skPoint(sketch, "E706.MirrorCS.start.orphan", {"position": v(-216.39, -454.79) * mm});
            skLineSegment(sketch, "E707", {"start": v(-216.39, -449.79) * mm, "end": v(-216.39, -454.79) * mm});
            skPoint(sketch, "E708.orphan", {"position": v(-388.13, -662.13) * mm});
            skPoint(sketch, "E709.MirrorP", {"position": v(-14.64, -662.13) * mm});
            skPoint(sketch, "E710.orphan", {"position": v(-383.13, -662.13) * mm});
            skLineSegment(sketch, "E711", {"start": v(-14.64, -506.13) * mm, "end": v(-4.64, -506.13) * mm});
            skLineSegment(sketch, "E712", {"start": v(-4.64, -612.13) * mm, "end": v(-14.64, -612.13) * mm});
            skLineSegment(sketch, "E713", {"start": v(-14.64, -532.17) * mm, "end": v(-4.64, -532.17) * mm});
            skLineSegment(sketch, "E714", {"start": v(-14.64, -552.17) * mm, "end": v(-4.64, -552.17) * mm});
            skLineSegment(sketch, "E715", {"start": v(-14.64, -592.13) * mm, "end": v(-4.64, -592.13) * mm});
            skPoint(sketch, "E716.MirrorCS.end.orphan", {"position": v(-19.64, -532.17) * mm});
            skPoint(sketch, "E717.MirrorCS.end.orphan", {"position": v(-19.64, -552.17) * mm});
            skLineSegment(sketch, "E718.bottom", {"start": v(-14.64, -638.13) * mm, "end": v(-4.64, -638.13) * mm});
            skLineSegment(sketch, "E718.top", {"start": v(-14.64, -612.13) * mm, "end": v(-4.64, -612.13) * mm});
            skLineSegment(sketch, "E718.right", {"start": v(-4.64, -638.13) * mm, "end": v(-4.64, -612.13) * mm});
            skLineSegment(sketch, "E719", {"start": v(-14.64, -651.58) * mm, "end": v(-14.64, -638.13) * mm});
            skPoint(sketch, "E720.MirrorCS.start.orphan", {"position": v(-19.64, -638.13) * mm});
            skPoint(sketch, "E721.MirrorCS.end.orphan", {"position": v(-19.64, -592.13) * mm});
            skPoint(sketch, "E722.MirrorCS.end.orphan", {"position": v(-19.64, -612.13) * mm});
            skLineSegment(sketch, "E723.trimOffspring", {"start": v(-4.64, -552.17) * mm, "end": v(-4.64, -592.13) * mm});
            skPoint(sketch, "E724.MirrorCS.end.orphan", {"position": v(-19.64, -482.13) * mm});
            skPoint(sketch, "E725.MirrorCS.start.orphan", {"position": v(-19.64, -506.13) * mm});
            skPoint(sketch, "E726.trimOffspring.start.orphan", {"position": v(-19.64, -662.13) * mm});
            skLineSegment(sketch, "E727", {"start": v(-14.64, -492.72) * mm, "end": v(-14.64, -506.13) * mm});
            skLineSegment(sketch, "E728", {"start": v(-4.64, -506.13) * mm, "end": v(-4.64, -532.17) * mm});
            skLineSegment(sketch, "E729", {"start": v(-14.64, -532.17) * mm, "end": v(-14.64, -552.17) * mm});
            skLineSegment(sketch, "E730", {"start": v(-14.64, -592.13) * mm, "end": v(-14.64, -612.13) * mm});
            skLineSegment(sketch, "E731.MirrorCS", {"start": v(-298.13, -662.13) * mm, "end": v(-298.44, -662.13) * mm});
            skLineSegment(sketch, "E732.MirrorCS", {"start": v(-286.39, -592.13) * mm, "end": v(-291.39, -592.13) * mm});
            skLineSegment(sketch, "E733.MirrorCS", {"start": v(-293.13, -532.17) * mm, "end": v(-298.13, -532.17) * mm});
            skLineSegment(sketch, "E734.MirrorCS", {"start": v(-298.13, -612.13) * mm, "end": v(-293.13, -612.13) * mm});
            skLineSegment(sketch, "E735.MirrorCS", {"start": v(-291.39, -612.13) * mm, "end": v(-286.39, -612.13) * mm});
            skLineSegment(sketch, "E736.MirrorCS", {"start": v(-291.39, -638.13) * mm, "end": v(-286.39, -638.13) * mm});
            skLineSegment(sketch, "E737.MirrorCS", {"start": v(-291.39, -506.17) * mm, "end": v(-286.39, -506.17) * mm});
            skLineSegment(sketch, "E738.MirrorCS", {"start": v(-293.13, -506.17) * mm, "end": v(-298.13, -506.13) * mm});
            skLineSegment(sketch, "E739.MirrorCS", {"start": v(-286.39, -552.17) * mm, "end": v(-291.39, -552.17) * mm});
            skLineSegment(sketch, "E740.MirrorCS", {"start": v(-293.13, -638.13) * mm, "end": v(-298.13, -638.13) * mm});
            skLineSegment(sketch, "E741.MirrorCS", {"start": v(-291.39, -532.17) * mm, "end": v(-286.39, -532.17) * mm});
            skLineSegment(sketch, "E742.MirrorCS", {"start": v(-298.13, -552.17) * mm, "end": v(-293.13, -552.17) * mm});
            skLineSegment(sketch, "E743.MirrorCS", {"start": v(-293.13, -592.13) * mm, "end": v(-298.13, -592.13) * mm});
            skLineSegment(sketch, "E744.MirrorCS", {"start": v(-398.13, -612.13) * mm, "end": v(-388.13, -612.13) * mm});
            skLineSegment(sketch, "E745.MirrorCS", {"start": v(-293.13, -612.13) * mm, "end": v(-293.13, -638.13) * mm});
            skLineSegment(sketch, "E746.MirrorCS", {"start": v(-291.39, -572.17) * mm, "end": v(-286.39, -572.17) * mm});
            skLineSegment(sketch, "E747.MirrorCS", {"start": v(-298.13, -506.13) * mm, "end": v(-298.13, -482.13) * mm});
            skPoint(sketch, "E748.MirrorP", {"position": v(-298.13, -482.13) * mm});
            skPoint(sketch, "E749.MirrorP", {"position": v(-383.13, -506.13) * mm});
            skPoint(sketch, "E750.MirrorP", {"position": v(-383.13, -552.17) * mm});
            skLineSegment(sketch, "E751.MirrorCS", {"start": v(-293.13, -552.13) * mm, "end": v(-293.13, -592.13) * mm});
            skLineSegment(sketch, "E752.MirrorCS", {"start": v(-388.13, -612.13) * mm, "end": v(-398.13, -612.13) * mm});
            skPoint(sketch, "E753.MirrorP", {"position": v(-383.13, -532.17) * mm});
            skLineSegment(sketch, "E754.MirrorCS", {"start": v(-293.13, -506.17) * mm, "end": v(-293.13, -532.17) * mm});
            skLineSegment(sketch, "E755.MirrorCS", {"start": v(-388.13, -651.58) * mm, "end": v(-388.13, -638.13) * mm});
            skLineSegment(sketch, "E756.MirrorCS", {"start": v(-388.13, -552.17) * mm, "end": v(-398.13, -552.17) * mm});
            skLineSegment(sketch, "E757.MirrorCS", {"start": v(-291.39, -552.17) * mm, "end": v(-291.39, -592.13) * mm});
            skLineSegment(sketch, "E758.MirrorCS", {"start": v(-388.13, -532.17) * mm, "end": v(-398.13, -532.17) * mm});
            skLineSegment(sketch, "E759.MirrorCS", {"start": v(-388.13, -506.13) * mm, "end": v(-398.13, -506.13) * mm});
            skPoint(sketch, "E760.MirrorP", {"position": v(-383.13, -638.13) * mm});
            skPoint(sketch, "E761.MirrorP", {"position": v(-383.13, -482.13) * mm});
            skLineSegment(sketch, "E762.MirrorCS", {"start": v(-388.13, -492.72) * mm, "end": v(-388.13, -506.13) * mm});
            skLineSegment(sketch, "E763.MirrorCS", {"start": v(-398.13, -552.17) * mm, "end": v(-398.13, -592.13) * mm});
            skLineSegment(sketch, "E764.MirrorCS", {"start": v(-286.39, -612.13) * mm, "end": v(-286.39, -638.13) * mm});
            skPoint(sketch, "E765.MirrorP", {"position": v(-383.13, -592.13) * mm});
            skPoint(sketch, "E766.MirrorP", {"position": v(-298.13, -662.13) * mm});
            skLineSegment(sketch, "E767.MirrorCS", {"start": v(-298.13, -532.17) * mm, "end": v(-298.13, -552.17) * mm});
            skLineSegment(sketch, "E768.MirrorCS", {"start": v(-291.39, -612.13) * mm, "end": v(-291.39, -638.13) * mm});
            skLineSegment(sketch, "E769.MirrorCS", {"start": v(-291.39, -506.17) * mm, "end": v(-291.39, -532.17) * mm});
            skLineSegment(sketch, "E770.MirrorCS", {"start": v(-286.39, -506.17) * mm, "end": v(-286.39, -532.17) * mm});
            skLineSegment(sketch, "E771.MirrorCS", {"start": v(-298.13, -638.13) * mm, "end": v(-298.13, -662.13) * mm});
            skLineSegment(sketch, "E772.MirrorCS", {"start": v(-398.13, -506.13) * mm, "end": v(-398.13, -532.17) * mm});
            skLineSegment(sketch, "E773.MirrorCS", {"start": v(-388.13, -532.17) * mm, "end": v(-388.13, -552.17) * mm});
            skPoint(sketch, "E774.MirrorP", {"position": v(-383.13, -612.13) * mm});
            skLineSegment(sketch, "E775.MirrorCS", {"start": v(-388.13, -592.13) * mm, "end": v(-388.13, -612.13) * mm});
            skLineSegment(sketch, "E776.MirrorCS", {"start": v(-388.13, -592.13) * mm, "end": v(-398.13, -592.13) * mm});
            skLineSegment(sketch, "E777.MirrorCS", {"start": v(-286.39, -572.17) * mm, "end": v(-286.39, -552.17) * mm});
            skLineSegment(sketch, "E778.MirrorCS", {"start": v(-298.13, -592.13) * mm, "end": v(-298.13, -612.13) * mm});
            skLineSegment(sketch, "E779.MirrorCS", {"start": v(-286.39, -572.17) * mm, "end": v(-286.39, -592.13) * mm});
            skLineSegment(sketch, "E780.MirrorCS", {"start": v(-388.13, -638.13) * mm, "end": v(-398.13, -638.13) * mm});
            skLineSegment(sketch, "E781.MirrorCS", {"start": v(-398.13, -638.13) * mm, "end": v(-398.13, -612.13) * mm});
            skLineSegment(sketch, "E782", {"start": v(-286.39, -638.13) * mm, "end": v(-286.39, -657.13) * mm});
            skLineSegment(sketch, "E783", {"start": v(-286.39, -657.13) * mm, "end": v(-267.39, -657.13) * mm});
            skLineSegment(sketch, "E784", {"start": v(-267.39, -657.13) * mm, "end": v(-241.39, -657.13) * mm});
            skLineSegment(sketch, "E785", {"start": v(-221.39, -657.13) * mm, "end": v(-181.39, -657.13) * mm});
            skLineSegment(sketch, "E786", {"start": v(-161.39, -657.13) * mm, "end": v(-135.39, -657.13) * mm});
            skLineSegment(sketch, "E787", {"start": v(-267.39, -657.13) * mm, "end": v(-267.39, -662.13) * mm});
            skLineSegment(sketch, "E788", {"start": v(-135.39, -662.13) * mm, "end": v(-135.39, -657.13) * mm});
            skLineSegment(sketch, "E789.bottom", {"start": v(-241.39, -657.13) * mm, "end": v(-267.39, -657.13) * mm});
            skLineSegment(sketch, "E789.top", {"start": v(-241.39, -662.13) * mm, "end": v(-267.39, -662.13) * mm});
            skLineSegment(sketch, "E789.left", {"start": v(-241.39, -657.13) * mm, "end": v(-241.39, -662.13) * mm});
            skLineSegment(sketch, "E790.top", {"start": v(-161.39, -662.13) * mm, "end": v(-135.39, -662.13) * mm});
            skLineSegment(sketch, "E790.left", {"start": v(-161.39, -657.13) * mm, "end": v(-161.39, -662.13) * mm});
            skLineSegment(sketch, "E790.right", {"start": v(-135.39, -657.13) * mm, "end": v(-135.39, -662.13) * mm});
            skLineSegment(sketch, "E791", {"start": v(-221.39, -657.13) * mm, "end": v(-221.39, -662.13) * mm});
            skLineSegment(sketch, "E792", {"start": v(-223.39, -359.79) * mm, "end": v(-223.39, -449.79) * mm});
            skLineSegment(sketch, "E793.left", {"start": v(-221.39, -662.13) * mm, "end": v(-221.39, -657.13) * mm});
            skLineSegment(sketch, "E793.right", {"start": v(-181.39, -662.13) * mm, "end": v(-181.39, -657.13) * mm});
            skLineSegment(sketch, "E794.bottom", {"start": v(-221.39, -662.13) * mm, "end": v(-181.39, -662.13) * mm});
            skLineSegment(sketch, "E795.MirrorCS", {"start": v(-210.93, -844.22) * mm, "end": v(-205.93, -844.22) * mm});
            skLineSegment(sketch, "E796.MirrorCS", {"start": v(-205.93, -798.22) * mm, "end": v(-210.93, -798.22) * mm});
            skLineSegment(sketch, "E797.MirrorCS", {"start": v(-205.93, -824.22) * mm, "end": v(-210.93, -824.22) * mm});
            skLineSegment(sketch, "E798.MirrorCS", {"start": v(-210.93, -884.18) * mm, "end": v(-205.93, -884.18) * mm});
            skLineSegment(sketch, "E799.MirrorCS", {"start": v(-205.93, -904.18) * mm, "end": v(-210.93, -904.18) * mm});
            skLineSegment(sketch, "E800.MirrorCS", {"start": v(-205.93, -930.18) * mm, "end": v(-210.93, -930.18) * mm});
            skLineSegment(sketch, "E801.MirrorCS", {"start": v(-205.93, -864.22) * mm, "end": v(-210.93, -864.22) * mm});
            skLineSegment(sketch, "E802.MirrorCS", {"start": v(-210.93, -904.18) * mm, "end": v(-210.93, -930.18) * mm});
            skLineSegment(sketch, "E803.MirrorCS", {"start": v(-210.93, -864.22) * mm, "end": v(-210.93, -844.22) * mm});
            skLineSegment(sketch, "E804.MirrorCS", {"start": v(-210.93, -864.22) * mm, "end": v(-210.93, -884.18) * mm});
            skLineSegment(sketch, "E805.MirrorCS", {"start": v(-205.93, -798.22) * mm, "end": v(-205.93, -824.22) * mm});
            skLineSegment(sketch, "E806.MirrorCS", {"start": v(-210.93, -798.22) * mm, "end": v(-210.93, -824.22) * mm});
            skLineSegment(sketch, "E807.MirrorCS", {"start": v(-205.93, -904.18) * mm, "end": v(-205.93, -930.18) * mm});
            skLineSegment(sketch, "E808.MirrorCS", {"start": v(-205.93, -844.22) * mm, "end": v(-205.93, -884.18) * mm});
            skLineSegment(sketch, "E809.MirrorCS", {"start": v(-199.2, -798.18) * mm, "end": v(-199.2, -780.18) * mm});
            skLineSegment(sketch, "E810.MirrorCS", {"start": v(-204.2, -798.22) * mm, "end": v(-199.2, -798.18) * mm});
            skLineSegment(sketch, "E811.MirrorCS", {"start": v(-204.2, -798.22) * mm, "end": v(-204.2, -824.22) * mm});
            skLineSegment(sketch, "E812.MirrorCS", {"start": v(-204.2, -824.22) * mm, "end": v(-199.2, -824.22) * mm});
            skLineSegment(sketch, "E813.MirrorCS", {"start": v(-199.2, -824.22) * mm, "end": v(-199.2, -844.22) * mm});
            skLineSegment(sketch, "E814.MirrorCS", {"start": v(-199.2, -844.22) * mm, "end": v(-204.2, -844.22) * mm});
            skLineSegment(sketch, "E815.MirrorCS", {"start": v(-204.2, -844.18) * mm, "end": v(-204.2, -884.18) * mm});
            skLineSegment(sketch, "E816.MirrorCS", {"start": v(-204.2, -884.18) * mm, "end": v(-199.2, -884.18) * mm});
            skLineSegment(sketch, "E817.MirrorCS", {"start": v(-199.2, -884.18) * mm, "end": v(-199.2, -904.18) * mm});
            skLineSegment(sketch, "E818.MirrorCS", {"start": v(-199.2, -904.18) * mm, "end": v(-204.2, -904.18) * mm});
            skLineSegment(sketch, "E819.MirrorCS", {"start": v(-204.2, -904.18) * mm, "end": v(-204.2, -930.18) * mm});
            skLineSegment(sketch, "E820.MirrorCS", {"start": v(-204.2, -930.18) * mm, "end": v(-199.2, -930.18) * mm});
            skLineSegment(sketch, "E821.MirrorCS", {"start": v(-199.2, -930.18) * mm, "end": v(-199.2, -948.26) * mm});
            skLineSegment(sketch, "E822", {"start": v(-199.2, -954.18) * mm, "end": v(-198.88, -954.18) * mm});
            skLineSegment(sketch, "E823.MirrorCS", {"start": v(-198.88, -954.18) * mm, "end": v(-199.2, -954.22) * mm});
            skLineSegment(sketch, "E824", {"start": v(-109.2, -798.18) * mm, "end": v(-99.2, -798.18) * mm});
            skLineSegment(sketch, "E825", {"start": v(-99.2, -904.18) * mm, "end": v(-109.2, -904.18) * mm});
            skLineSegment(sketch, "E826", {"start": v(-109.2, -824.22) * mm, "end": v(-99.2, -824.22) * mm});
            skLineSegment(sketch, "E827", {"start": v(-109.2, -844.22) * mm, "end": v(-99.2, -844.22) * mm});
            skLineSegment(sketch, "E828", {"start": v(-109.2, -884.18) * mm, "end": v(-99.2, -884.18) * mm});
            skPoint(sketch, "E829.MirrorCS.end.orphan", {"position": v(-114.2, -824.22) * mm});
            skPoint(sketch, "E830.MirrorCS.end.orphan", {"position": v(-114.2, -844.22) * mm});
            skLineSegment(sketch, "E831.bottom", {"start": v(-109.2, -930.18) * mm, "end": v(-99.2, -930.18) * mm});
            skLineSegment(sketch, "E831.top", {"start": v(-109.2, -904.18) * mm, "end": v(-99.2, -904.18) * mm});
            skLineSegment(sketch, "E831.right", {"start": v(-99.2, -930.18) * mm, "end": v(-99.2, -904.18) * mm});
            skLineSegment(sketch, "E832", {"start": v(-109.2, -938.67) * mm, "end": v(-109.2, -930.18) * mm});
            skPoint(sketch, "E833.MirrorCS.start.orphan", {"position": v(-114.2, -930.18) * mm});
            skPoint(sketch, "E834.MirrorCS.end.orphan", {"position": v(-114.2, -884.18) * mm});
            skPoint(sketch, "E835.MirrorCS.end.orphan", {"position": v(-114.2, -904.18) * mm});
            skLineSegment(sketch, "E836.trimOffspring", {"start": v(-99.2, -844.22) * mm, "end": v(-99.2, -884.18) * mm});
            skPoint(sketch, "E837.MirrorCS.start.orphan", {"position": v(-114.2, -798.18) * mm});
            skLineSegment(sketch, "E838", {"start": v(-109.2, -789.77) * mm, "end": v(-109.2, -798.18) * mm});
            skLineSegment(sketch, "E839", {"start": v(-99.2, -798.18) * mm, "end": v(-99.2, -824.22) * mm});
            skLineSegment(sketch, "E840", {"start": v(-109.2, -824.22) * mm, "end": v(-109.2, -844.22) * mm});
            skLineSegment(sketch, "E841", {"start": v(-109.2, -884.18) * mm, "end": v(-109.2, -904.18) * mm});
            skPoint(sketch, "E842.start.orphan", {"position": v(-109.2, -784.77) * mm});
            skPoint(sketch, "E843.orphan", {"position": v(-109.2, -943.63) * mm});
            skLineSegment(sketch, "E844", {"start": v(-256.43, -371.03) * mm, "end": v(-256.43, -371.03) * mm});
            skLineSegment(sketch, "E845.trimOffspring", {"start": v(-256.43, -371.03) * mm, "end": v(-261.39, -371.03) * mm});
            skLineSegment(sketch, "E846", {"start": v(-216.39, -359.79) * mm, "end": v(-216.39, -354.79) * mm});
            skLineSegment(sketch, "E847", {"start": v(-206.39, -354.79) * mm, "end": v(-206.39, -359.79) * mm});
            skLineSegment(sketch, "E848", {"start": v(-206.39, -359.79) * mm, "end": v(-201.39, -359.79) * mm});
            skLineSegment(sketch, "E849.MirrorCS", {"start": v(-196.39, -359.79) * mm, "end": v(-201.39, -359.79) * mm});
            skLineSegment(sketch, "E850.MirrorCS", {"start": v(-186.39, -359.79) * mm, "end": v(-186.39, -354.79) * mm});
            skLineSegment(sketch, "E851.MirrorCS", {"start": v(-196.39, -354.79) * mm, "end": v(-196.39, -359.79) * mm});
            skPoint(sketch, "E852.MirrorCS.start.orphan", {"position": v(-177.4, -371.03) * mm});
            skLineSegment(sketch, "E853", {"start": v(-246.39, -361.03) * mm, "end": v(-241.39, -361.03) * mm});
            skLineSegment(sketch, "E854", {"start": v(-206.39, -354.79) * mm, "end": v(-206.39, -349.79) * mm});
            skLineSegment(sketch, "E855", {"start": v(-206.39, -349.79) * mm, "end": v(-216.39, -349.79) * mm});
            skLineSegment(sketch, "E856", {"start": v(-216.39, -349.79) * mm, "end": v(-216.39, -354.79) * mm});
            skLineSegment(sketch, "E857.MirrorCS", {"start": v(-196.39, -354.79) * mm, "end": v(-196.39, -349.79) * mm});
            skLineSegment(sketch, "E858.MirrorCS", {"start": v(-196.39, -349.79) * mm, "end": v(-186.39, -349.79) * mm});
            skLineSegment(sketch, "E859.MirrorCS", {"start": v(-186.39, -349.79) * mm, "end": v(-186.39, -354.79) * mm});
            skLineSegment(sketch, "E860", {"start": v(-271.39, -487.13) * mm, "end": v(-276.39, -487.13) * mm});
            skLineSegment(sketch, "E861", {"start": v(-276.39, -487.13) * mm, "end": v(-276.39, -482.13) * mm});
            skLineSegment(sketch, "E862.bottom", {"start": v(-276.39, -487.13) * mm, "end": v(-261.39, -487.13) * mm});
            skLineSegment(sketch, "E862.top", {"start": v(-276.39, -482.13) * mm, "end": v(-261.39, -482.13) * mm});
            skLineSegment(sketch, "E862.right", {"start": v(-261.39, -487.13) * mm, "end": v(-261.39, -482.13) * mm});
            skLineSegment(sketch, "E863", {"start": v(-246.39, -487.13) * mm, "end": v(-246.39, -482.13) * mm});
            skLineSegment(sketch, "E864", {"start": v(-246.39, -482.13) * mm, "end": v(-231.39, -482.13) * mm});
            skLineSegment(sketch, "E865.bottom", {"start": v(-241.39, -487.13) * mm, "end": v(-231.39, -487.13) * mm});
            skLineSegment(sketch, "E865.top", {"start": v(-241.39, -482.13) * mm, "end": v(-231.39, -482.13) * mm});
            skLineSegment(sketch, "E865.right", {"start": v(-231.39, -487.13) * mm, "end": v(-231.39, -482.13) * mm});
            skPoint(sketch, "E649.right.start.orphan", {"position": v(-241.39, -482.13) * mm});
            skLineSegment(sketch, "E866.MirrorCS", {"start": v(-276.39, -461) * mm, "end": v(-276.39, -466) * mm});
            skPoint(sketch, "E867.MirrorP", {"position": v(-241.39, -466) * mm});
            skLineSegment(sketch, "E868.MirrorCS", {"start": v(-241.39, -466) * mm, "end": v(-231.39, -466) * mm});
            skPoint(sketch, "E869.MirrorP", {"position": v(-257, -461) * mm});
            skLineSegment(sketch, "E870.MirrorCS", {"start": v(-246.39, -466) * mm, "end": v(-231.39, -466) * mm});
            skPoint(sketch, "E871.MirrorP", {"position": v(-235.17, -461) * mm});
            skLineSegment(sketch, "E872.MirrorCS", {"start": v(-246.39, -461) * mm, "end": v(-246.39, -466) * mm});
            skLineSegment(sketch, "E873.MirrorCS", {"start": v(-261.39, -461) * mm, "end": v(-261.39, -466) * mm});
            skPoint(sketch, "E874.MirrorP", {"position": v(-256.39, -461) * mm});
            skPoint(sketch, "E875.MirrorP", {"position": v(-235.17, -466) * mm});
            skLineSegment(sketch, "E876.MirrorCS", {"start": v(-276.39, -466) * mm, "end": v(-261.39, -466) * mm});
            skLineSegment(sketch, "E877.MirrorCS", {"start": v(-231.39, -461) * mm, "end": v(-231.39, -466) * mm});
            skPoint(sketch, "E878.MirrorP", {"position": v(-260.78, -461) * mm});
            skLineSegment(sketch, "E879", {"start": v(-284.39, -461) * mm, "end": v(-276.39, -461) * mm});
            skPoint(sketch, "E880.orphan", {"position": v(-276.39, -466) * mm});
            skPoint(sketch, "E881.start.orphan", {"position": v(-276.39, -474.06) * mm});
            skLineSegment(sketch, "E882", {"start": v(-257, -461) * mm, "end": v(-246.39, -461) * mm});
            skLineSegment(sketch, "E883", {"start": v(-261.39, -461) * mm, "end": v(-257, -461) * mm});
            skLineSegment(sketch, "E884", {"start": v(-231.39, -461) * mm, "end": v(-225.37, -461.03) * mm});
            skLineSegment(sketch, "E885.MirrorCS", {"start": v(-131.39, -487.13) * mm, "end": v(-126.39, -487.13) * mm});
            skLineSegment(sketch, "E886.MirrorCS", {"start": v(-126.39, -487.13) * mm, "end": v(-126.39, -482.13) * mm});
            skLineSegment(sketch, "E887.MirrorCS", {"start": v(-126.39, -482.13) * mm, "end": v(-131.39, -482.13) * mm});
            skPoint(sketch, "E888.MirrorP", {"position": v(-161.39, -482.13) * mm});
            skPoint(sketch, "E889.MirrorP", {"position": v(-141.39, -487.13) * mm});
            skLineSegment(sketch, "E890.MirrorCS", {"start": v(-141.39, -487.13) * mm, "end": v(-141.39, -482.13) * mm});
            skLineSegment(sketch, "E891.MirrorCS", {"start": v(-126.39, -482.13) * mm, "end": v(-141.39, -482.13) * mm});
            skPoint(sketch, "E892.MirrorP", {"position": v(-126.39, -474.06) * mm});
            skPoint(sketch, "E893.MirrorP", {"position": v(-167.61, -482.13) * mm});
            skLineSegment(sketch, "E894.MirrorCS", {"start": v(-156.39, -482.13) * mm, "end": v(-171.39, -482.13) * mm});
            skLineSegment(sketch, "E895.MirrorCS", {"start": v(-171.39, -487.13) * mm, "end": v(-171.39, -482.13) * mm});
            skLineSegment(sketch, "E896.MirrorCS", {"start": v(-156.39, -487.13) * mm, "end": v(-161.39, -487.13) * mm});
            skLineSegment(sketch, "E897.MirrorCS", {"start": v(-156.39, -487.13) * mm, "end": v(-156.39, -482.13) * mm});
            skPoint(sketch, "E898.MirrorP", {"position": v(-167.61, -487.13) * mm});
            skLineSegment(sketch, "E899.MirrorCS", {"start": v(-161.39, -482.13) * mm, "end": v(-171.39, -482.13) * mm});
            skLineSegment(sketch, "E900.MirrorCS", {"start": v(-161.39, -487.13) * mm, "end": v(-171.39, -487.13) * mm});
            skLineSegment(sketch, "E901.MirrorCS", {"start": v(-126.39, -487.13) * mm, "end": v(-141.39, -487.13) * mm});
            skPoint(sketch, "E902.start.orphan", {"position": v(-271.39, -482.13) * mm});
            skPoint(sketch, "E903.MirrorCS.start.orphan", {"position": v(-131.39, -482.13) * mm});
            skLineSegment(sketch, "E904", {"start": v(-298.13, -662.13) * mm, "end": v(-388.13, -662.13) * mm});
            skLineSegment(sketch, "E905", {"start": v(-388.13, -662.13) * mm, "end": v(-388.13, -651.58) * mm});
            skLineSegment(sketch, "E906", {"start": v(-298.13, -482.13) * mm, "end": v(-383.13, -482.13) * mm});
            skLineSegment(sketch, "E907", {"start": v(-388.13, -492.72) * mm, "end": v(-388.13, -482.13) * mm});
            skLineSegment(sketch, "E908", {"start": v(-388.13, -482.13) * mm, "end": v(-383.13, -482.13) * mm});
            skPoint(sketch, "E909.MirrorCS.start.orphan", {"position": v(-383.13, -492.13) * mm});
            skLineSegment(sketch, "E910", {"start": v(-286.39, -461) * mm, "end": v(-286.39, -371.03) * mm});
            skLineSegment(sketch, "E911", {"start": v(-286.39, -371.03) * mm, "end": v(-276.39, -371.03) * mm});
            skLineSegment(sketch, "E912", {"start": v(-276.39, -371.03) * mm, "end": v(-276.39, -361.03) * mm});
            skLineSegment(sketch, "E913", {"start": v(-276.39, -361.03) * mm, "end": v(-261.39, -361.03) * mm});
            skLineSegment(sketch, "E914", {"start": v(-261.39, -361.03) * mm, "end": v(-261.39, -371.03) * mm});
            skLineSegment(sketch, "E915", {"start": v(-261.39, -371.03) * mm, "end": v(-246.39, -371.03) * mm});
            skLineSegment(sketch, "E916", {"start": v(-246.39, -371.03) * mm, "end": v(-246.39, -361.03) * mm});
            skLineSegment(sketch, "E917", {"start": v(-246.39, -361.03) * mm, "end": v(-231.39, -361.03) * mm});
            skLineSegment(sketch, "E918", {"start": v(-231.39, -361.03) * mm, "end": v(-231.39, -371.03) * mm});
            skLineSegment(sketch, "E919", {"start": v(-231.39, -371.03) * mm, "end": v(-225.37, -371.03) * mm});
            skPoint(sketch, "E920.end.orphan", {"position": v(-256.39, -361.03) * mm});
            skPoint(sketch, "E921.orphan", {"position": v(-256.43, -366.05) * mm});
            skPoint(sketch, "E922.orphan", {"position": v(-241.39, -371.03) * mm});
            skPoint(sketch, "E923.end.orphan", {"position": v(-241.39, -366.03) * mm});
            skPoint(sketch, "E924.trimOffspring.end.orphan", {"position": v(-286.39, -371.03) * mm});
            skLineSegment(sketch, "E925.MirrorCS", {"start": v(-146.34, -371.03) * mm, "end": v(-146.34, -371.03) * mm});
            skLineSegment(sketch, "E926.MirrorCS", {"start": v(-126.39, -461) * mm, "end": v(-126.39, -466) * mm});
            skLineSegment(sketch, "E927.MirrorCS", {"start": v(-156.39, -466) * mm, "end": v(-161.39, -466) * mm});
            skLineSegment(sketch, "E928.MirrorCS", {"start": v(-126.39, -466) * mm, "end": v(-131.39, -466) * mm});
            skLineSegment(sketch, "E929.MirrorCS", {"start": v(-146.34, -371.03) * mm, "end": v(-141.39, -371.03) * mm});
            skLineSegment(sketch, "E930.MirrorCS", {"start": v(-141.39, -461) * mm, "end": v(-145.78, -461) * mm});
            skLineSegment(sketch, "E931.MirrorCS", {"start": v(-141.39, -461) * mm, "end": v(-141.39, -466) * mm});
            skLineSegment(sketch, "E932.MirrorCS", {"start": v(-156.39, -461) * mm, "end": v(-156.39, -466) * mm});
            skLineSegment(sketch, "E933.MirrorCS", {"start": v(-118.39, -461) * mm, "end": v(-116.39, -461) * mm});
            skLineSegment(sketch, "E934.MirrorCS", {"start": v(-161.39, -466) * mm, "end": v(-171.39, -466) * mm});
            skLineSegment(sketch, "E935.MirrorCS", {"start": v(-171.39, -461) * mm, "end": v(-171.39, -466) * mm});
            skLineSegment(sketch, "E936.MirrorCS", {"start": v(-156.39, -466) * mm, "end": v(-171.39, -466) * mm});
            skLineSegment(sketch, "E937.MirrorCS", {"start": v(-156.39, -361.03) * mm, "end": v(-161.39, -361.03) * mm});
            skPoint(sketch, "E938.MirrorP", {"position": v(-146.39, -461) * mm});
            skPoint(sketch, "E939.MirrorP", {"position": v(-161.39, -466) * mm});
            skPoint(sketch, "E940.MirrorP", {"position": v(-146.34, -366.05) * mm});
            skPoint(sketch, "E941.MirrorP", {"position": v(-126.39, -466) * mm});
            skLineSegment(sketch, "E942.MirrorCS", {"start": v(-126.39, -361.03) * mm, "end": v(-141.39, -361.03) * mm});
            skLineSegment(sketch, "E943.MirrorCS", {"start": v(-171.39, -361.03) * mm, "end": v(-171.39, -371.03) * mm});
            skLineSegment(sketch, "E944.MirrorCS", {"start": v(-126.39, -371.03) * mm, "end": v(-126.39, -361.03) * mm});
            skLineSegment(sketch, "E945.MirrorCS", {"start": v(-126.39, -466) * mm, "end": v(-141.39, -466) * mm});
            skPoint(sketch, "E946.MirrorP", {"position": v(-116.39, -371.03) * mm});
            skPoint(sketch, "E947.MirrorP", {"position": v(-146.39, -361.03) * mm});
            skPoint(sketch, "E948.MirrorP", {"position": v(-142, -461) * mm});
            skLineSegment(sketch, "E949.MirrorCS", {"start": v(-171.39, -461) * mm, "end": v(-177.4, -461.03) * mm});
            skLineSegment(sketch, "E950.MirrorCS", {"start": v(-145.78, -461) * mm, "end": v(-156.39, -461) * mm});
            skLineSegment(sketch, "E951.MirrorCS", {"start": v(-118.39, -461) * mm, "end": v(-126.39, -461) * mm});
            skLineSegment(sketch, "E952.MirrorCS", {"start": v(-116.39, -461) * mm, "end": v(-116.39, -371.03) * mm});
            skLineSegment(sketch, "E953.MirrorCS", {"start": v(-156.39, -371.03) * mm, "end": v(-156.39, -361.03) * mm});
            skPoint(sketch, "E954.MirrorP", {"position": v(-145.78, -461) * mm});
            skPoint(sketch, "E955.MirrorP", {"position": v(-161.39, -371.03) * mm});
            skLineSegment(sketch, "E956.MirrorCS", {"start": v(-156.39, -361.03) * mm, "end": v(-171.39, -361.03) * mm});
            skPoint(sketch, "E957.MirrorP", {"position": v(-167.61, -466) * mm});
            skLineSegment(sketch, "E958.MirrorCS", {"start": v(-141.39, -371.03) * mm, "end": v(-156.39, -371.03) * mm});
            skLineSegment(sketch, "E959.MirrorCS", {"start": v(-171.39, -371.03) * mm, "end": v(-177.4, -371.03) * mm});
            skLineSegment(sketch, "E960.MirrorCS", {"start": v(-141.39, -361.03) * mm, "end": v(-141.39, -371.03) * mm});
            skLineSegment(sketch, "E961.MirrorCS", {"start": v(-116.39, -371.03) * mm, "end": v(-126.39, -371.03) * mm});
            skPoint(sketch, "E962.MirrorP", {"position": v(-167.61, -461) * mm});
            skPoint(sketch, "E963.MirrorP", {"position": v(-161.39, -366.03) * mm});
            skLineSegment(sketch, "E964.MirrorCS", {"start": v(-14.64, -482.13) * mm, "end": v(-19.64, -482.13) * mm});
            skLineSegment(sketch, "E965.MirrorCS", {"start": v(-14.64, -662.13) * mm, "end": v(-14.64, -651.58) * mm});
            skLineSegment(sketch, "E966.MirrorCS", {"start": v(-14.64, -492.72) * mm, "end": v(-14.64, -482.13) * mm});
            skLineSegment(sketch, "E967.MirrorCS", {"start": v(-104.64, -662.13) * mm, "end": v(-14.64, -662.13) * mm});
            skPoint(sketch, "E968.MirrorP", {"position": v(-19.64, -492.13) * mm});
            skLineSegment(sketch, "E969.MirrorCS", {"start": v(-104.64, -482.13) * mm, "end": v(-19.64, -482.13) * mm});
            skLineSegment(sketch, "E970", {"start": v(-199.2, -780.18) * mm, "end": v(-199.2, -779.18) * mm});
            skLineSegment(sketch, "E971", {"start": v(-199.2, -779.18) * mm, "end": v(-109.2, -779.18) * mm});
            skLineSegment(sketch, "E972", {"start": v(-109.2, -779.18) * mm, "end": v(-109.2, -789.77) * mm});
            skLineSegment(sketch, "E973.MirrorCS", {"start": v(-199.2, -948.26) * mm, "end": v(-199.2, -949.26) * mm});
            skLineSegment(sketch, "E974.MirrorCS", {"start": v(-199.2, -949.26) * mm, "end": v(-109.2, -949.26) * mm});
            skLineSegment(sketch, "E975.MirrorCS", {"start": v(-109.2, -949.26) * mm, "end": v(-109.2, -938.67) * mm});
            skPoint(sketch, "E976.end.orphan", {"position": v(374.89, -989.25) * mm});
            skPoint(sketch, "E977.end.orphan", {"position": v(338.65, -1021.08) * mm});
            skCircle(sketch, "E978", {"center": v(309.87, -1090.2) * mm, "radius": 7.1 * mm});
            skLineSegment(sketch, "E979.MirrorCS", {"start": v(459.89, -1001.12) * mm, "end": v(464.89, -1001.12) * mm});
            skLineSegment(sketch, "E980.MirrorCS", {"start": v(464.89, -955.12) * mm, "end": v(459.89, -955.12) * mm});
            skLineSegment(sketch, "E981.MirrorCS", {"start": v(464.89, -981.12) * mm, "end": v(459.89, -981.12) * mm});
            skLineSegment(sketch, "E982.MirrorCS", {"start": v(459.89, -1041.08) * mm, "end": v(464.89, -1041.08) * mm});
            skLineSegment(sketch, "E983.MirrorCS", {"start": v(464.89, -1061.08) * mm, "end": v(459.89, -1061.08) * mm});
            skLineSegment(sketch, "E984.MirrorCS", {"start": v(464.89, -1087.08) * mm, "end": v(459.89, -1087.08) * mm});
            skLineSegment(sketch, "E985.MirrorCS", {"start": v(459.89, -1061.08) * mm, "end": v(459.89, -1087.08) * mm});
            skLineSegment(sketch, "E986.MirrorCS", {"start": v(459.89, -1021.12) * mm, "end": v(459.89, -1001.12) * mm});
            skLineSegment(sketch, "E987.MirrorCS", {"start": v(459.89, -1021.12) * mm, "end": v(459.89, -1041.08) * mm});
            skLineSegment(sketch, "E988.MirrorCS", {"start": v(464.89, -955.12) * mm, "end": v(464.89, -981.12) * mm});
            skLineSegment(sketch, "E989.MirrorCS", {"start": v(459.89, -955.12) * mm, "end": v(459.89, -981.12) * mm});
            skLineSegment(sketch, "E990.MirrorCS", {"start": v(464.89, -1061.08) * mm, "end": v(464.89, -1087.08) * mm});
            skLineSegment(sketch, "E991.MirrorCS", {"start": v(464.89, -1001.12) * mm, "end": v(464.89, -1041.08) * mm});
            skPoint(sketch, "E992.start.orphan", {"position": v(314.89, -936.08) * mm});
            skPoint(sketch, "E993.start.orphan", {"position": v(341.1, -931.08) * mm});
            skPoint(sketch, "E994.left.start.orphan", {"position": v(341.1, -936.08) * mm});
            skLineSegment(sketch, "E995.bottom", {"start": v(299.89, -931.08) * mm, "end": v(304.89, -931.08) * mm});
            skLineSegment(sketch, "E996.top", {"start": v(329.89, -936.08) * mm, "end": v(334.89, -936.08) * mm});
            skLineSegment(sketch, "E997.bottom", {"start": v(389.89, -914.1) * mm, "end": v(379.89, -914.1) * mm});
            skLineSegment(sketch, "E997.top", {"start": v(389.89, -909.1) * mm, "end": v(379.89, -909.1) * mm});
            skLineSegment(sketch, "E997.left", {"start": v(369.89, -914.1) * mm, "end": v(369.89, -909.1) * mm});
            skLineSegment(sketch, "E997.right", {"start": v(389.89, -914.1) * mm, "end": v(389.89, -909.1) * mm});
            skLineSegment(sketch, "E998.MirrorCS", {"start": v(379.89, -914.1) * mm, "end": v(379.89, -909.1) * mm});
            skLineSegment(sketch, "E999.MirrorCS", {"start": v(359.89, -914.1) * mm, "end": v(359.89, -909.1) * mm});
            skLineSegment(sketch, "E1000.trimOffspring", {"start": v(359.89, -909.1) * mm, "end": v(369.89, -909.1) * mm});
            skCircle(sketch, "E1001", {"center": v(374.89, -1021.1) * mm, "radius": 70 * mm});
            skPoint(sketch, "E1002.MirrorCS.start.orphan", {"position": v(471.63, -931.08) * mm});
            skLineSegment(sketch, "E1003.MirrorCS", {"start": v(289.89, -1041.08) * mm, "end": v(284.89, -1041.08) * mm});
            skLineSegment(sketch, "E1004.MirrorCS", {"start": v(284.89, -1061.08) * mm, "end": v(289.89, -1061.08) * mm});
            skLineSegment(sketch, "E1005.MirrorCS", {"start": v(284.89, -1087.08) * mm, "end": v(289.89, -1087.08) * mm});
            skLineSegment(sketch, "E1006.MirrorCS", {"start": v(284.89, -955.12) * mm, "end": v(289.89, -955.12) * mm});
            skLineSegment(sketch, "E1007.MirrorCS", {"start": v(289.89, -1001.12) * mm, "end": v(284.89, -1001.12) * mm});
            skLineSegment(sketch, "E1008.MirrorCS", {"start": v(284.89, -981.12) * mm, "end": v(289.89, -981.12) * mm});
            skLineSegment(sketch, "E1009.MirrorCS", {"start": v(284.89, -1001.12) * mm, "end": v(284.89, -1041.08) * mm});
            skLineSegment(sketch, "E1010.MirrorCS", {"start": v(289.89, -1061.08) * mm, "end": v(289.89, -1087.08) * mm});
            skLineSegment(sketch, "E1011.MirrorCS", {"start": v(284.89, -1061.08) * mm, "end": v(284.89, -1087.08) * mm});
            skLineSegment(sketch, "E1012.MirrorCS", {"start": v(284.89, -955.12) * mm, "end": v(284.89, -981.12) * mm});
            skLineSegment(sketch, "E1013.MirrorCS", {"start": v(289.89, -955.12) * mm, "end": v(289.89, -981.12) * mm});
            skLineSegment(sketch, "E1014.MirrorCS", {"start": v(289.89, -1021.12) * mm, "end": v(289.89, -1001.12) * mm});
            skLineSegment(sketch, "E1015.MirrorCS", {"start": v(289.89, -1021.12) * mm, "end": v(289.89, -1041.08) * mm});
            skLineSegment(sketch, "E1016", {"start": v(308.89, -1106.08) * mm, "end": v(334.89, -1106.08) * mm});
            skLineSegment(sketch, "E1017", {"start": v(354.89, -1106.08) * mm, "end": v(394.89, -1106.08) * mm});
            skLineSegment(sketch, "E1018", {"start": v(414.89, -1106.08) * mm, "end": v(440.89, -1106.08) * mm});
            skLineSegment(sketch, "E1019", {"start": v(308.89, -1106.08) * mm, "end": v(308.89, -1111.08) * mm});
            skLineSegment(sketch, "E1020", {"start": v(440.89, -1111.08) * mm, "end": v(440.89, -1106.08) * mm});
            skLineSegment(sketch, "E1021.bottom", {"start": v(334.89, -1106.08) * mm, "end": v(308.89, -1106.08) * mm});
            skLineSegment(sketch, "E1021.top", {"start": v(334.89, -1111.08) * mm, "end": v(308.89, -1111.08) * mm});
            skLineSegment(sketch, "E1021.left", {"start": v(334.89, -1106.08) * mm, "end": v(334.89, -1111.08) * mm});
            skLineSegment(sketch, "E1022.top", {"start": v(414.89, -1111.08) * mm, "end": v(440.89, -1111.08) * mm});
            skLineSegment(sketch, "E1022.left", {"start": v(414.89, -1106.08) * mm, "end": v(414.89, -1111.08) * mm});
            skLineSegment(sketch, "E1022.right", {"start": v(440.89, -1106.08) * mm, "end": v(440.89, -1111.08) * mm});
            skLineSegment(sketch, "E1023", {"start": v(354.89, -1106.08) * mm, "end": v(354.89, -1111.08) * mm});
            skLineSegment(sketch, "E1024.left", {"start": v(354.89, -1111.08) * mm, "end": v(354.89, -1106.08) * mm});
            skLineSegment(sketch, "E1024.right", {"start": v(394.89, -1111.08) * mm, "end": v(394.89, -1106.08) * mm});
            skLineSegment(sketch, "E1025.bottom", {"start": v(354.89, -1111.08) * mm, "end": v(394.89, -1111.08) * mm});
            skLineSegment(sketch, "E1026", {"start": v(304.89, -936.08) * mm, "end": v(299.89, -936.08) * mm});
            skLineSegment(sketch, "E1027", {"start": v(299.89, -936.08) * mm, "end": v(299.89, -931.08) * mm});
            skLineSegment(sketch, "E1028.bottom", {"start": v(299.89, -936.08) * mm, "end": v(314.89, -936.08) * mm});
            skLineSegment(sketch, "E1028.top", {"start": v(299.89, -931.08) * mm, "end": v(314.89, -931.08) * mm});
            skLineSegment(sketch, "E1028.right", {"start": v(314.89, -936.08) * mm, "end": v(314.89, -931.08) * mm});
            skLineSegment(sketch, "E1029", {"start": v(329.89, -936.08) * mm, "end": v(329.89, -931.08) * mm});
            skLineSegment(sketch, "E1030", {"start": v(329.89, -931.08) * mm, "end": v(344.89, -931.08) * mm});
            skLineSegment(sketch, "E1031.bottom", {"start": v(334.89, -936.08) * mm, "end": v(344.89, -936.08) * mm});
            skLineSegment(sketch, "E1031.top", {"start": v(334.89, -931.08) * mm, "end": v(344.89, -931.08) * mm});
            skLineSegment(sketch, "E1031.right", {"start": v(344.89, -936.08) * mm, "end": v(344.89, -931.08) * mm});
            skPoint(sketch, "E1032.start.orphan", {"position": v(334.28, -931.08) * mm});
            skPoint(sketch, "E996.right.start.orphan", {"position": v(334.89, -931.08) * mm});
            skPoint(sketch, "E1033.start.orphan", {"position": v(299.89, -923.01) * mm});
            skLineSegment(sketch, "E1034.MirrorCS", {"start": v(444.89, -936.08) * mm, "end": v(449.89, -936.08) * mm});
            skLineSegment(sketch, "E1035.MirrorCS", {"start": v(449.89, -936.08) * mm, "end": v(449.89, -931.08) * mm});
            skLineSegment(sketch, "E1036.MirrorCS", {"start": v(449.89, -931.08) * mm, "end": v(444.89, -931.08) * mm});
            skPoint(sketch, "E1037.MirrorP", {"position": v(415.5, -931.08) * mm});
            skPoint(sketch, "E1038.MirrorP", {"position": v(414.89, -931.08) * mm});
            skPoint(sketch, "E1039.MirrorP", {"position": v(434.89, -936.08) * mm});
            skLineSegment(sketch, "E1040.MirrorCS", {"start": v(434.89, -936.08) * mm, "end": v(434.89, -931.08) * mm});
            skLineSegment(sketch, "E1041.MirrorCS", {"start": v(449.89, -931.08) * mm, "end": v(434.89, -931.08) * mm});
            skPoint(sketch, "E1042.MirrorP", {"position": v(449.89, -923.01) * mm});
            skPoint(sketch, "E1043.MirrorP", {"position": v(408.66, -931.08) * mm});
            skLineSegment(sketch, "E1044.MirrorCS", {"start": v(419.89, -931.08) * mm, "end": v(404.89, -931.08) * mm});
            skLineSegment(sketch, "E1045.MirrorCS", {"start": v(404.89, -936.08) * mm, "end": v(404.89, -931.08) * mm});
            skLineSegment(sketch, "E1046.MirrorCS", {"start": v(419.89, -936.08) * mm, "end": v(414.89, -936.08) * mm});
            skLineSegment(sketch, "E1047.MirrorCS", {"start": v(419.89, -936.08) * mm, "end": v(419.89, -931.08) * mm});
            skPoint(sketch, "E1048.MirrorP", {"position": v(408.66, -936.08) * mm});
            skLineSegment(sketch, "E1049.MirrorCS", {"start": v(414.89, -931.08) * mm, "end": v(404.89, -931.08) * mm});
            skLineSegment(sketch, "E1050.MirrorCS", {"start": v(414.89, -936.08) * mm, "end": v(404.89, -936.08) * mm});
            skLineSegment(sketch, "E1051.MirrorCS", {"start": v(449.89, -936.08) * mm, "end": v(434.89, -936.08) * mm});
            skPoint(sketch, "E1052.start.orphan", {"position": v(304.89, -931.08) * mm});
            skPoint(sketch, "E1053.MirrorCS.start.orphan", {"position": v(444.89, -931.08) * mm});
            skLineSegment(sketch, "E1054", {"start": v(308.89, -1116.08) * mm, "end": v(284.89, -1116.08) * mm});
            skLineSegment(sketch, "E1055", {"start": v(279.89, -1111.08) * mm, "end": v(279.89, -1021.12) * mm});
            skLineSegment(sketch, "E1056.bottom", {"start": v(464.89, -926.08) * mm, "end": v(399.89, -926.08) * mm});
            skLineSegment(sketch, "E1056.top", {"start": v(464.89, -1116.08) * mm, "end": v(284.89, -1116.08) * mm});
            skLineSegment(sketch, "E1056.right", {"start": v(279.89, -931.08) * mm, "end": v(279.89, -1111.08) * mm});
            skPoint(sketch, "E1057.end.orphan", {"position": v(449.89, -926.08) * mm});
            skLineSegment(sketch, "E1058.0", {"start": v(394.89, -914.1) * mm, "end": v(394.89, -909.1) * mm});
            skLineSegment(sketch, "E1059", {"start": v(394.89, -909.1) * mm, "end": v(394.89, -919.1) * mm});
            skLineSegment(sketch, "E1060", {"start": v(394.89, -919.1) * mm, "end": v(394.89, -921.08) * mm});
            skLineSegment(sketch, "E1061.trimOffspring", {"start": v(349.89, -926.08) * mm, "end": v(284.89, -926.08) * mm});
            skLineSegment(sketch, "E1062", {"start": v(464.89, -926.08) * mm, "end": v(464.89, -926.08) * mm});
            skLineSegment(sketch, "E1063", {"start": v(469.89, -931.08) * mm, "end": v(469.89, -1111.08) * mm});
            skLineSegment(sketch, "E1064", {"start": v(464.89, -1116.08) * mm, "end": v(464.89, -1116.08) * mm});
            skLineSegment(sketch, "E1065.top", {"start": v(359.89, -904.1) * mm, "end": v(389.89, -904.1) * mm});
            skLineSegment(sketch, "E1065.left", {"start": v(354.89, -921.08) * mm, "end": v(354.89, -909.1) * mm});
            skLineSegment(sketch, "E1065.right", {"start": v(394.89, -921.08) * mm, "end": v(394.89, -909.1) * mm});
            skLineSegment(sketch, "E1066.bottom", {"start": v(359.89, -914.1) * mm, "end": v(369.89, -914.1) * mm});
            skPoint(sketch, "E1067.visualSharp", {"position": v(394.89, -904.1) * mm});
            skArc(sketch, "E1067.filletArc", {"start": v(394.89, -909.1) * mm, "mid": v(393.42, -905.57) * mm, "end": v(389.89, -904.1) * mm});
            skPoint(sketch, "E1068.visualSharp", {"position": v(354.89, -904.1) * mm});
            skArc(sketch, "E1068.filletArc", {"start": v(359.89, -904.1) * mm, "mid": v(356.35, -905.57) * mm, "end": v(354.89, -909.1) * mm});
            skPoint(sketch, "E1069.visualSharp", {"position": v(354.89, -926.08) * mm});
            skArc(sketch, "E1069.filletArc", {"start": v(349.89, -926.08) * mm, "mid": v(353.42, -924.62) * mm, "end": v(354.89, -921.08) * mm});
            skPoint(sketch, "E1070.visualSharp", {"position": v(279.89, -926.08) * mm});
            skArc(sketch, "E1070.filletArc", {"start": v(284.89, -926.08) * mm, "mid": v(281.35, -927.55) * mm, "end": v(279.89, -931.08) * mm});
            skPoint(sketch, "E1071.visualSharp", {"position": v(279.89, -1116.08) * mm});
            skArc(sketch, "E1071.filletArc", {"start": v(279.89, -1111.08) * mm, "mid": v(281.35, -1114.62) * mm, "end": v(284.89, -1116.08) * mm});
            skPoint(sketch, "E1072.visualSharp", {"position": v(469.89, -1116.08) * mm});
            skArc(sketch, "E1072.filletArc", {"start": v(464.89, -1116.08) * mm, "mid": v(468.42, -1114.62) * mm, "end": v(469.89, -1111.08) * mm});
            skPoint(sketch, "E1073.visualSharp", {"position": v(469.89, -926.08) * mm});
            skArc(sketch, "E1073.filletArc", {"start": v(469.89, -931.08) * mm, "mid": v(468.42, -927.55) * mm, "end": v(464.89, -926.08) * mm});
            skPoint(sketch, "E1074.visualSharp", {"position": v(394.89, -926.08) * mm});
            skArc(sketch, "E1074.filletArc", {"start": v(394.89, -921.08) * mm, "mid": v(396.35, -924.62) * mm, "end": v(399.89, -926.08) * mm});
            skPoint(sketch, "E1075.end.orphan", {"position": v(554.4, -720.62) * mm});
            skPoint(sketch, "E1076.end.orphan", {"position": v(518.17, -752.46) * mm});
            skCircle(sketch, "E1077", {"center": v(489.39, -821.58) * mm, "radius": 7.1 * mm});
            skLineSegment(sketch, "E1078.MirrorCS", {"start": v(639.4, -732.5) * mm, "end": v(644.4, -732.5) * mm});
            skLineSegment(sketch, "E1079.MirrorCS", {"start": v(644.4, -686.5) * mm, "end": v(639.4, -686.5) * mm});
            skLineSegment(sketch, "E1080.MirrorCS", {"start": v(644.4, -712.5) * mm, "end": v(639.4, -712.5) * mm});
            skLineSegment(sketch, "E1081.MirrorCS", {"start": v(639.4, -772.46) * mm, "end": v(644.4, -772.46) * mm});
            skLineSegment(sketch, "E1082.MirrorCS", {"start": v(644.4, -792.46) * mm, "end": v(639.4, -792.46) * mm});
            skLineSegment(sketch, "E1083.MirrorCS", {"start": v(644.4, -818.46) * mm, "end": v(639.4, -818.46) * mm});
            skLineSegment(sketch, "E1084.MirrorCS", {"start": v(639.4, -792.46) * mm, "end": v(639.4, -818.46) * mm});
            skLineSegment(sketch, "E1085.MirrorCS", {"start": v(639.4, -752.5) * mm, "end": v(639.4, -732.5) * mm});
            skLineSegment(sketch, "E1086.MirrorCS", {"start": v(639.4, -752.5) * mm, "end": v(639.4, -772.46) * mm});
            skLineSegment(sketch, "E1087.MirrorCS", {"start": v(644.4, -686.5) * mm, "end": v(644.4, -712.5) * mm});
            skLineSegment(sketch, "E1088.MirrorCS", {"start": v(639.4, -686.5) * mm, "end": v(639.4, -712.5) * mm});
            skLineSegment(sketch, "E1089.MirrorCS", {"start": v(644.4, -792.46) * mm, "end": v(644.4, -818.46) * mm});
            skLineSegment(sketch, "E1090.MirrorCS", {"start": v(644.4, -732.5) * mm, "end": v(644.4, -772.46) * mm});
            skPoint(sketch, "E1091.start.orphan", {"position": v(494.4, -667.46) * mm});
            skPoint(sketch, "E1092.start.orphan", {"position": v(520.62, -662.46) * mm});
            skPoint(sketch, "E1093.left.start.orphan", {"position": v(520.62, -667.46) * mm});
            skLineSegment(sketch, "E1094.bottom", {"start": v(479.4, -662.46) * mm, "end": v(484.4, -662.46) * mm});
            skLineSegment(sketch, "E1095.top", {"start": v(509.4, -667.46) * mm, "end": v(514.4, -667.46) * mm});
            skLineSegment(sketch, "E1096.bottom", {"start": v(569.4, -645.48) * mm, "end": v(559.4, -645.48) * mm});
            skLineSegment(sketch, "E1096.top", {"start": v(569.4, -640.48) * mm, "end": v(559.4, -640.48) * mm});
            skLineSegment(sketch, "E1096.left", {"start": v(549.4, -645.48) * mm, "end": v(549.4, -640.48) * mm});
            skLineSegment(sketch, "E1096.right", {"start": v(569.4, -645.48) * mm, "end": v(569.4, -640.48) * mm});
            skLineSegment(sketch, "E1097.MirrorCS", {"start": v(559.4, -645.48) * mm, "end": v(559.4, -640.48) * mm});
            skLineSegment(sketch, "E1098.MirrorCS", {"start": v(539.4, -645.48) * mm, "end": v(539.4, -640.48) * mm});
            skLineSegment(sketch, "E1099.trimOffspring", {"start": v(539.4, -640.48) * mm, "end": v(549.4, -640.48) * mm});
            skPoint(sketch, "E1100.MirrorCS.start.orphan", {"position": v(651.14, -662.46) * mm});
            skLineSegment(sketch, "E1101.MirrorCS", {"start": v(469.4, -772.46) * mm, "end": v(464.4, -772.46) * mm});
            skLineSegment(sketch, "E1102.MirrorCS", {"start": v(464.4, -792.46) * mm, "end": v(469.4, -792.46) * mm});
            skLineSegment(sketch, "E1103.MirrorCS", {"start": v(464.4, -818.46) * mm, "end": v(469.4, -818.46) * mm});
            skLineSegment(sketch, "E1104.MirrorCS", {"start": v(464.4, -686.5) * mm, "end": v(469.4, -686.5) * mm});
            skLineSegment(sketch, "E1105.MirrorCS", {"start": v(469.4, -732.5) * mm, "end": v(464.4, -732.5) * mm});
            skLineSegment(sketch, "E1106.MirrorCS", {"start": v(464.4, -712.5) * mm, "end": v(469.4, -712.5) * mm});
            skLineSegment(sketch, "E1107.MirrorCS", {"start": v(464.4, -732.5) * mm, "end": v(464.4, -772.46) * mm});
            skLineSegment(sketch, "E1108.MirrorCS", {"start": v(469.4, -792.46) * mm, "end": v(469.4, -818.46) * mm});
            skLineSegment(sketch, "E1109.MirrorCS", {"start": v(464.4, -792.46) * mm, "end": v(464.4, -818.46) * mm});
            skLineSegment(sketch, "E1110.MirrorCS", {"start": v(464.4, -686.5) * mm, "end": v(464.4, -712.5) * mm});
            skLineSegment(sketch, "E1111.MirrorCS", {"start": v(469.4, -686.5) * mm, "end": v(469.4, -712.5) * mm});
            skLineSegment(sketch, "E1112.MirrorCS", {"start": v(469.4, -752.5) * mm, "end": v(469.4, -732.5) * mm});
            skLineSegment(sketch, "E1113.MirrorCS", {"start": v(469.4, -752.5) * mm, "end": v(469.4, -772.46) * mm});
            skLineSegment(sketch, "E1114", {"start": v(488.4, -837.46) * mm, "end": v(514.4, -837.46) * mm});
            skLineSegment(sketch, "E1115", {"start": v(534.4, -837.46) * mm, "end": v(574.4, -837.46) * mm});
            skLineSegment(sketch, "E1116", {"start": v(594.4, -837.46) * mm, "end": v(620.4, -837.46) * mm});
            skLineSegment(sketch, "E1117", {"start": v(488.4, -837.46) * mm, "end": v(488.4, -842.46) * mm});
            skLineSegment(sketch, "E1118", {"start": v(620.4, -842.46) * mm, "end": v(620.4, -837.46) * mm});
            skLineSegment(sketch, "E1119.bottom", {"start": v(514.4, -837.46) * mm, "end": v(488.4, -837.46) * mm});
            skLineSegment(sketch, "E1119.top", {"start": v(514.4, -842.46) * mm, "end": v(488.4, -842.46) * mm});
            skLineSegment(sketch, "E1119.left", {"start": v(514.4, -837.46) * mm, "end": v(514.4, -842.46) * mm});
            skLineSegment(sketch, "E1120.top", {"start": v(594.4, -842.46) * mm, "end": v(620.4, -842.46) * mm});
            skLineSegment(sketch, "E1120.left", {"start": v(594.4, -837.46) * mm, "end": v(594.4, -842.46) * mm});
            skLineSegment(sketch, "E1120.right", {"start": v(620.4, -837.46) * mm, "end": v(620.4, -842.46) * mm});
            skLineSegment(sketch, "E1121", {"start": v(534.4, -837.46) * mm, "end": v(534.4, -842.46) * mm});
            skLineSegment(sketch, "E1122.left", {"start": v(534.4, -842.46) * mm, "end": v(534.4, -837.46) * mm});
            skLineSegment(sketch, "E1122.right", {"start": v(574.4, -842.46) * mm, "end": v(574.4, -837.46) * mm});
            skLineSegment(sketch, "E1123.bottom", {"start": v(534.4, -842.46) * mm, "end": v(574.4, -842.46) * mm});
            skLineSegment(sketch, "E1124", {"start": v(484.4, -667.46) * mm, "end": v(479.4, -667.46) * mm});
            skLineSegment(sketch, "E1125", {"start": v(479.4, -667.46) * mm, "end": v(479.4, -662.46) * mm});
            skLineSegment(sketch, "E1126.bottom", {"start": v(479.4, -667.46) * mm, "end": v(494.4, -667.46) * mm});
            skLineSegment(sketch, "E1126.top", {"start": v(479.4, -662.46) * mm, "end": v(494.4, -662.46) * mm});
            skLineSegment(sketch, "E1126.right", {"start": v(494.4, -667.46) * mm, "end": v(494.4, -662.46) * mm});
            skLineSegment(sketch, "E1127", {"start": v(509.4, -667.46) * mm, "end": v(509.4, -662.46) * mm});
            skLineSegment(sketch, "E1128", {"start": v(509.4, -662.46) * mm, "end": v(524.4, -662.46) * mm});
            skLineSegment(sketch, "E1129.bottom", {"start": v(514.4, -667.46) * mm, "end": v(524.4, -667.46) * mm});
            skLineSegment(sketch, "E1129.top", {"start": v(514.4, -662.46) * mm, "end": v(524.4, -662.46) * mm});
            skLineSegment(sketch, "E1129.right", {"start": v(524.4, -667.46) * mm, "end": v(524.4, -662.46) * mm});
            skPoint(sketch, "E1130.start.orphan", {"position": v(513.79, -662.46) * mm});
            skPoint(sketch, "E1095.right.start.orphan", {"position": v(514.4, -662.46) * mm});
            skPoint(sketch, "E1131.start.orphan", {"position": v(479.4, -654.39) * mm});
            skLineSegment(sketch, "E1132.MirrorCS", {"start": v(624.4, -667.46) * mm, "end": v(629.4, -667.46) * mm});
            skLineSegment(sketch, "E1133.MirrorCS", {"start": v(629.4, -667.46) * mm, "end": v(629.4, -662.46) * mm});
            skLineSegment(sketch, "E1134.MirrorCS", {"start": v(629.4, -662.46) * mm, "end": v(624.4, -662.46) * mm});
            skPoint(sketch, "E1135.MirrorP", {"position": v(595.01, -662.46) * mm});
            skPoint(sketch, "E1136.MirrorP", {"position": v(594.4, -662.46) * mm});
            skPoint(sketch, "E1137.MirrorP", {"position": v(614.4, -667.46) * mm});
            skLineSegment(sketch, "E1138.MirrorCS", {"start": v(614.4, -667.46) * mm, "end": v(614.4, -662.46) * mm});
            skLineSegment(sketch, "E1139.MirrorCS", {"start": v(629.4, -662.46) * mm, "end": v(614.4, -662.46) * mm});
            skPoint(sketch, "E1140.MirrorP", {"position": v(629.4, -654.39) * mm});
            skPoint(sketch, "E1141.MirrorP", {"position": v(588.18, -662.46) * mm});
            skLineSegment(sketch, "E1142.MirrorCS", {"start": v(599.4, -662.46) * mm, "end": v(584.4, -662.46) * mm});
            skLineSegment(sketch, "E1143.MirrorCS", {"start": v(584.4, -667.46) * mm, "end": v(584.4, -662.46) * mm});
            skLineSegment(sketch, "E1144.MirrorCS", {"start": v(599.4, -667.46) * mm, "end": v(594.4, -667.46) * mm});
            skLineSegment(sketch, "E1145.MirrorCS", {"start": v(599.4, -667.46) * mm, "end": v(599.4, -662.46) * mm});
            skPoint(sketch, "E1146.MirrorP", {"position": v(588.18, -667.46) * mm});
            skLineSegment(sketch, "E1147.MirrorCS", {"start": v(594.4, -662.46) * mm, "end": v(584.4, -662.46) * mm});
            skLineSegment(sketch, "E1148.MirrorCS", {"start": v(594.4, -667.46) * mm, "end": v(584.4, -667.46) * mm});
            skLineSegment(sketch, "E1149.MirrorCS", {"start": v(629.4, -667.46) * mm, "end": v(614.4, -667.46) * mm});
            skPoint(sketch, "E1150.start.orphan", {"position": v(484.4, -662.46) * mm});
            skPoint(sketch, "E1151.MirrorCS.start.orphan", {"position": v(624.4, -662.46) * mm});
            skLineSegment(sketch, "E1152", {"start": v(488.4, -847.46) * mm, "end": v(464.4, -847.46) * mm});
            skLineSegment(sketch, "E1153", {"start": v(459.4, -842.46) * mm, "end": v(459.4, -752.5) * mm});
            skLineSegment(sketch, "E1154.bottom", {"start": v(644.4, -657.46) * mm, "end": v(579.4, -657.46) * mm});
            skLineSegment(sketch, "E1154.top", {"start": v(644.4, -847.46) * mm, "end": v(464.4, -847.46) * mm});
            skLineSegment(sketch, "E1154.right", {"start": v(459.4, -662.46) * mm, "end": v(459.4, -842.46) * mm});
            skPoint(sketch, "E1155.end.orphan", {"position": v(629.4, -657.46) * mm});
            skLineSegment(sketch, "E1156.0", {"start": v(574.4, -645.48) * mm, "end": v(574.4, -640.48) * mm});
            skLineSegment(sketch, "E1157", {"start": v(574.4, -640.48) * mm, "end": v(574.4, -650.48) * mm});
            skLineSegment(sketch, "E1158", {"start": v(574.4, -650.48) * mm, "end": v(574.4, -652.46) * mm});
            skLineSegment(sketch, "E1159.trimOffspring", {"start": v(529.4, -657.46) * mm, "end": v(464.4, -657.46) * mm});
            skLineSegment(sketch, "E1160", {"start": v(644.4, -657.46) * mm, "end": v(644.4, -657.46) * mm});
            skLineSegment(sketch, "E1161", {"start": v(649.4, -662.46) * mm, "end": v(649.4, -842.46) * mm});
            skLineSegment(sketch, "E1162", {"start": v(644.4, -847.46) * mm, "end": v(644.4, -847.46) * mm});
            skLineSegment(sketch, "E1163.top", {"start": v(539.4, -635.48) * mm, "end": v(569.4, -635.48) * mm});
            skLineSegment(sketch, "E1163.left", {"start": v(534.4, -652.46) * mm, "end": v(534.4, -640.48) * mm});
            skLineSegment(sketch, "E1163.right", {"start": v(574.4, -652.46) * mm, "end": v(574.4, -640.48) * mm});
            skLineSegment(sketch, "E1164.bottom", {"start": v(539.4, -645.48) * mm, "end": v(549.4, -645.48) * mm});
            skPoint(sketch, "E1165.visualSharp", {"position": v(574.4, -635.48) * mm});
            skArc(sketch, "E1165.filletArc", {"start": v(574.4, -640.48) * mm, "mid": v(572.93, -636.94) * mm, "end": v(569.4, -635.48) * mm});
            skPoint(sketch, "E1166.visualSharp", {"position": v(534.4, -635.48) * mm});
            skArc(sketch, "E1166.filletArc", {"start": v(539.4, -635.48) * mm, "mid": v(535.86, -636.94) * mm, "end": v(534.4, -640.48) * mm});
            skPoint(sketch, "E1167.visualSharp", {"position": v(534.4, -657.46) * mm});
            skArc(sketch, "E1167.filletArc", {"start": v(529.4, -657.46) * mm, "mid": v(532.93, -656) * mm, "end": v(534.4, -652.46) * mm});
            skPoint(sketch, "E1168.visualSharp", {"position": v(459.4, -657.46) * mm});
            skArc(sketch, "E1168.filletArc", {"start": v(464.4, -657.46) * mm, "mid": v(460.86, -658.92) * mm, "end": v(459.4, -662.46) * mm});
            skPoint(sketch, "E1169.visualSharp", {"position": v(459.4, -847.46) * mm});
            skArc(sketch, "E1169.filletArc", {"start": v(459.4, -842.46) * mm, "mid": v(460.86, -846) * mm, "end": v(464.4, -847.46) * mm});
            skPoint(sketch, "E1170.visualSharp", {"position": v(649.4, -847.46) * mm});
            skArc(sketch, "E1170.filletArc", {"start": v(644.4, -847.46) * mm, "mid": v(647.93, -846) * mm, "end": v(649.4, -842.46) * mm});
            skPoint(sketch, "E1171.visualSharp", {"position": v(649.4, -657.46) * mm});
            skArc(sketch, "E1171.filletArc", {"start": v(649.4, -662.46) * mm, "mid": v(647.93, -658.92) * mm, "end": v(644.4, -657.46) * mm});
            skPoint(sketch, "E1172.visualSharp", {"position": v(574.4, -657.46) * mm});
            skArc(sketch, "E1172.filletArc", {"start": v(574.4, -652.46) * mm, "mid": v(575.86, -656) * mm, "end": v(579.4, -657.46) * mm});
            skSolve(sketch);
        }
        {
            var Q0;
            Q0=makeQuery(id+"F0.imprint","IMPRINT",FACE,{"disambiguationData":[TD([[makeQuery(id+"F0.imprint","IMPRINT",EDGE,{"derivedFrom":sQuery(id+"F0.wireOp",EDGE,"E78")}),-1.0]])]});
            var Q1;
            Q1=makeQuery(id+"F0.imprint","IMPRINT",FACE,{"disambiguationData":[TD([[makeQuery(id+"F0.imprint","IMPRINT",EDGE,{"derivedFrom":sQuery(id+"F0.wireOp",EDGE,"E456")}),-1.0]])]});
            var Q2;
            Q2=makeQuery(id+"F0.imprint","IMPRINT",FACE,{"disambiguationData":[TD([[makeQuery(id+"F0.imprint","IMPRINT",EDGE,{"derivedFrom":sQuery(id+"F0.wireOp",EDGE,"E26.MirrorCS")}),-1.0]])]});
            var Q3;
            {var subQ0=sQuery(id+"F0.wireOp",EDGE,"E4");Q3=makeQuery(id+"F0.imprint","IMPRINT",FACE,{"disambiguationData":[TD([[makeQuery(id+"F0.imprint","IMPRINT",EDGE,{"derivedFrom":subQ0}),1.0]])]});}
            var Q4;
            Q4=makeQuery(id+"F0.imprint","IMPRINT",FACE,{"disambiguationData":[TD([[makeQuery(id+"F0.imprint","IMPRINT",EDGE,{"derivedFrom":sQuery(id+"F0.wireOp",EDGE,"E330.MirrorCS")}),1.0]])]});
            var Q5;
            Q5=makeQuery(id+"F0.imprint","IMPRINT",FACE,{"disambiguationData":[TD([[makeQuery(id+"F0.imprint","IMPRINT",EDGE,{"derivedFrom":sQuery(id+"F0.wireOp",EDGE,"E49")}),1.0]])]});
            var Q6;
            Q6=makeQuery(id+"F0.imprint","IMPRINT",FACE,{"disambiguationData":[TD([[makeQuery(id+"F0.imprint","IMPRINT",EDGE,{"derivedFrom":sQuery(id+"F0.wireOp",EDGE,"E7")}),-1.0]])]});
            var Q7;
            Q7=makeQuery(id+"F0.imprint","IMPRINT",FACE,{"disambiguationData":[TD([[makeQuery(id+"F0.imprint","IMPRINT",EDGE,{"derivedFrom":sQuery(id+"F0.wireOp",EDGE,"E733.MirrorCS")}),-1.0]])]});
            var Q8;
            Q8=makeQuery(id+"F0.imprint","IMPRINT",FACE,{"disambiguationData":[TD([[makeQuery(id+"F0.imprint","IMPRINT",EDGE,{"derivedFrom":sQuery(id+"F0.wireOp",EDGE,"E656")}),-1.0]])]});
            var Q9;
            Q9=makeQuery(id+"F0.imprint","IMPRINT",FACE,{"disambiguationData":[TD([[makeQuery(id+"F0.imprint","IMPRINT",EDGE,{"derivedFrom":sQuery(id+"F0.wireOp",EDGE,"E661")}),-1.0]])]});
            var Q10;
            {var subQ10=sQuery(id+"F0.wireOp",EDGE,"E926.MirrorCS");Q10=makeQuery(id+"F0.imprint","IMPRINT",FACE,{"disambiguationData":[TD([[makeQuery(id+"F0.imprint","IMPRINT",EDGE,{"derivedFrom":subQ10}),-1.0]])]});}
            var Q11;
            Q11=makeQuery(id+"F0.imprint","IMPRINT",FACE,{"disambiguationData":[TD([[makeQuery(id+"F0.imprint","IMPRINT",EDGE,{"derivedFrom":sQuery(id+"F0.wireOp",EDGE,"E718.top")}),-1.0]])]});
            var Q12;
            Q12=makeQuery(id+"F0.imprint","IMPRINT",FACE,{"disambiguationData":[TD([[makeQuery(id+"F0.imprint","IMPRINT",EDGE,{"derivedFrom":sQuery(id+"F0.wireOp",EDGE,"E809.MirrorCS")}),-1.0]])]});
            var Q13;
            Q13=makeQuery(id+"F0.imprint","IMPRINT",FACE,{"disambiguationData":[TD([[makeQuery(id+"F0.imprint","IMPRINT",EDGE,{"derivedFrom":sQuery(id+"F0.wireOp",EDGE,"E1077")}),-1.0]])]});
            var Q14;
            Q14=makeQuery(id+"F0.imprint","IMPRINT",FACE,{"disambiguationData":[TD([[makeQuery(id+"F0.imprint","IMPRINT",EDGE,{"derivedFrom":sQuery(id+"F0.wireOp",EDGE,"E978")}),-1.0]])]});
            extrude(context, id + "F1", {"entities" : qUnion([Q0, Q1, Q2, Q3, Q4, Q5, Q6, Q7, Q8, Q9, Q10, Q11, Q12, Q13, Q14]), "depth" : 5 * mm, "offsetDistance" : 25 * mm});
        }
    });
